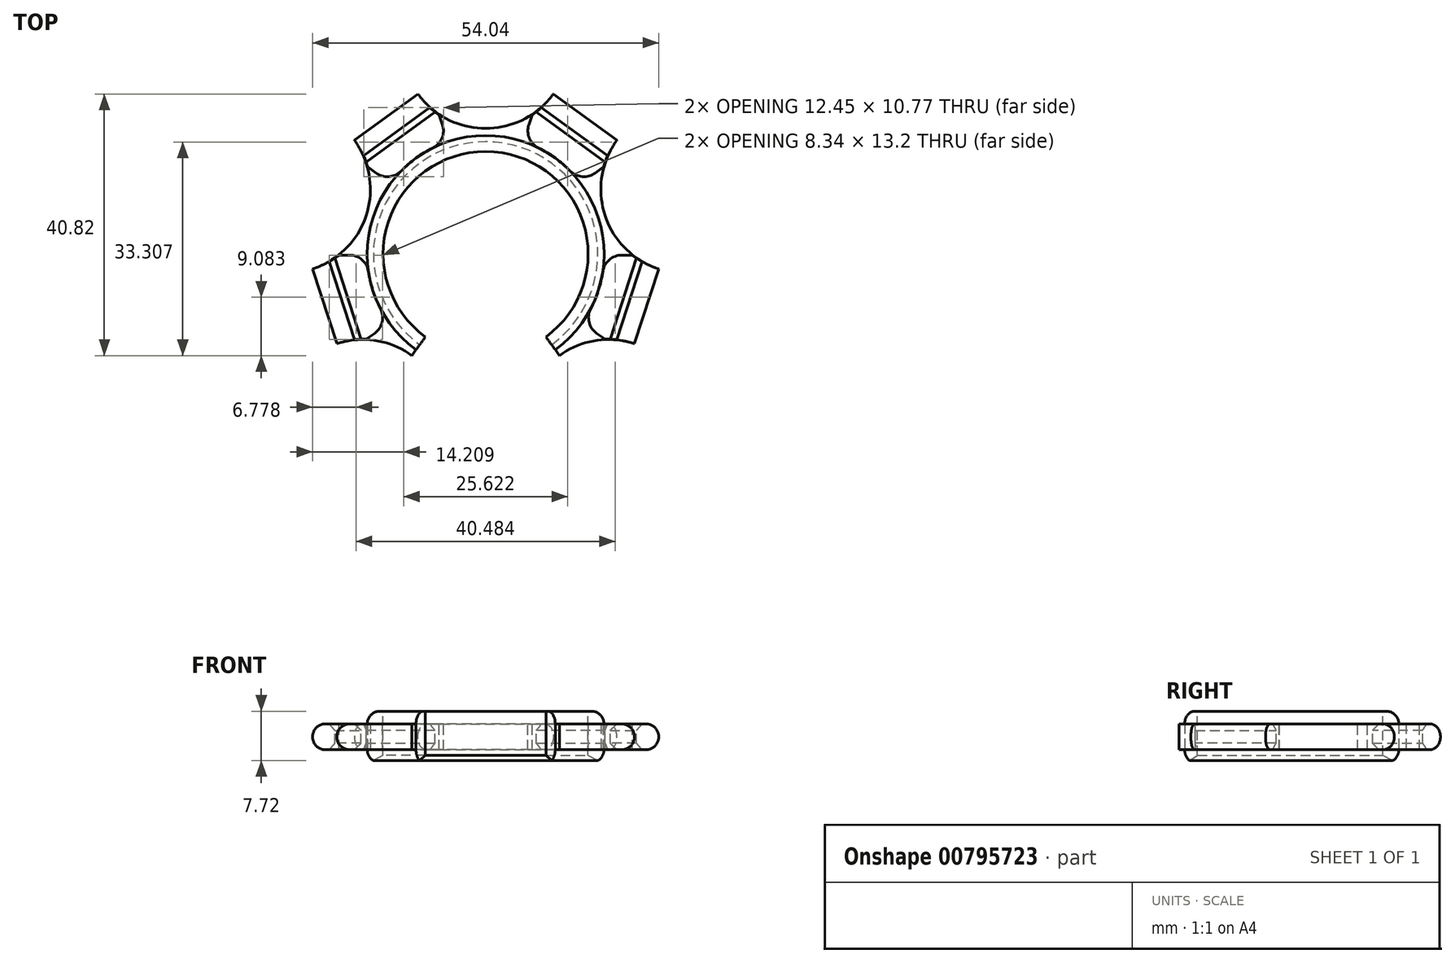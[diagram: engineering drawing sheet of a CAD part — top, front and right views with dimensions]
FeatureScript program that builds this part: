
annotation { "Feature Type Name" : "Feature", "Feature Type Description" : "" }
export const myFeature = defineFeature(function(context is Context, id is Id, definition is map)
    precondition{}
    {
        {
            var Q0;
            Q0=qCreatedBy(makeId("Top.planeOp"),FACE);
            var sketch = newSketch(context, id + "F0", { "sketchPlane" : qUnion([Q0])});
            skCircle(sketch, "E0.cCircle", {"center": v(0, 0) * mm, "radius": 52.24 * mm, "construction": true});
            skLineSegment(sketch, "E0.0", {"start": v(-37.95, 52.24) * mm, "end": v(37.95, 52.24) * mm});
            skLineSegment(sketch, "E0.1", {"start": v(37.95, 52.24) * mm, "end": v(61.41, -19.95) * mm});
            skLineSegment(sketch, "E0.2", {"start": v(61.41, -19.95) * mm, "end": v(0, -64.57) * mm});
            skLineSegment(sketch, "E0.3", {"start": v(0, -64.57) * mm, "end": v(-61.41, -19.95) * mm});
            skLineSegment(sketch, "E0.4", {"start": v(-61.41, -19.95) * mm, "end": v(-37.95, 52.24) * mm});
            skPoint(sketch, "E0.0.midPoint", {"position": v(0, 52.24) * mm});
            skLineSegment(sketch, "E1", {"start": v(0, 0) * mm, "end": v(-49.68, 16.14) * mm});
            skLineSegment(sketch, "E2", {"start": v(-49.68, 16.14) * mm, "end": v(0, 52.24) * mm});
            skLineSegment(sketch, "E3", {"start": v(0, 52.24) * mm, "end": v(0, 0) * mm});
            skLineSegment(sketch, "E4", {"start": v(0, 0) * mm, "end": v(49.68, 16.14) * mm});
            skLineSegment(sketch, "E5", {"start": v(49.68, 16.14) * mm, "end": v(0, 52.24) * mm});
            skLineSegment(sketch, "E6", {"start": v(49.68, 16.14) * mm, "end": v(30.7, -42.26) * mm});
            skLineSegment(sketch, "E7", {"start": v(30.7, -42.26) * mm, "end": v(0, 0) * mm});
            skLineSegment(sketch, "E8", {"start": v(0, 0) * mm, "end": v(-30.7, -42.26) * mm});
            skLineSegment(sketch, "E9", {"start": v(-30.7, -42.26) * mm, "end": v(-49.68, 16.14) * mm});
            skLineSegment(sketch, "E10", {"start": v(-30.7, -42.26) * mm, "end": v(30.7, -42.26) * mm});
            skLineSegment(sketch, "E11", {"start": v(0, 0) * mm, "end": v(61.41, -19.95) * mm});
            skLineSegment(sketch, "E12", {"start": v(0, 0) * mm, "end": v(37.95, 52.24) * mm});
            skLineSegment(sketch, "E13", {"start": v(0, 0) * mm, "end": v(-37.95, 52.24) * mm});
            skLineSegment(sketch, "E14", {"start": v(0, 0) * mm, "end": v(-61.41, -19.95) * mm});
            skLineSegment(sketch, "E15", {"start": v(0, -42.26) * mm, "end": v(0, -64.57) * mm});
            skLineSegment(sketch, "E16", {"start": v(0, 0) * mm, "end": v(-24.84, 8.07) * mm});
            skLineSegment(sketch, "E17", {"start": v(-24.84, 8.07) * mm, "end": v(-49.68, 16.14) * mm});
            skLineSegment(sketch, "E18", {"start": v(-37.26, 12.1) * mm, "end": v(-49.68, 16.14) * mm});
            skLineSegment(sketch, "E19", {"start": v(-37.26, 12.1) * mm, "end": v(-24.84, 8.07) * mm});
            skLineSegment(sketch, "E20", {"start": v(0, 0) * mm, "end": v(0, 26.12) * mm});
            skLineSegment(sketch, "E21", {"start": v(0, 26.12) * mm, "end": v(0, 52.24) * mm});
            skLineSegment(sketch, "E22", {"start": v(0, 39.18) * mm, "end": v(0, 52.24) * mm});
            skLineSegment(sketch, "E23", {"start": v(0, 39.18) * mm, "end": v(0, 26.12) * mm});
            skLineSegment(sketch, "E24", {"start": v(0, 0) * mm, "end": v(24.84, 8.07) * mm});
            skLineSegment(sketch, "E25", {"start": v(24.84, 8.07) * mm, "end": v(49.68, 16.14) * mm});
            skLineSegment(sketch, "E26", {"start": v(37.26, 12.1) * mm, "end": v(24.84, 8.07) * mm});
            skLineSegment(sketch, "E27", {"start": v(0, 0) * mm, "end": v(15.35, -21.13) * mm});
            skLineSegment(sketch, "E28", {"start": v(15.35, -21.13) * mm, "end": v(30.7, -42.26) * mm});
            skLineSegment(sketch, "E29", {"start": v(30.7, -42.26) * mm, "end": v(23.03, -31.7) * mm});
            skLineSegment(sketch, "E30", {"start": v(23.03, -31.7) * mm, "end": v(15.35, -21.13) * mm});
            skLineSegment(sketch, "E31", {"start": v(0, 0) * mm, "end": v(-15.35, -21.13) * mm});
            skLineSegment(sketch, "E32", {"start": v(-15.35, -21.13) * mm, "end": v(-30.7, -42.26) * mm});
            skLineSegment(sketch, "E33", {"start": v(-30.7, -42.26) * mm, "end": v(-23.03, -31.7) * mm});
            skLineSegment(sketch, "E34", {"start": v(-23.03, -31.7) * mm, "end": v(-15.35, -21.13) * mm});
            skLineSegment(sketch, "E35", {"start": v(-31.05, 10.09) * mm, "end": v(-43.47, 14.12) * mm});
            skLineSegment(sketch, "E36", {"start": v(0, 32.65) * mm, "end": v(0, 45.7) * mm});
            skLineSegment(sketch, "E37", {"start": v(37.26, 12.1) * mm, "end": v(49.68, 16.14) * mm});
            skLineSegment(sketch, "E38", {"start": v(31.05, 10.09) * mm, "end": v(43.47, 14.12) * mm});
            skLineSegment(sketch, "E39", {"start": v(30.7, -42.26) * mm, "end": v(26.87, -36.98) * mm});
            skLineSegment(sketch, "E40", {"start": v(-30.7, -42.26) * mm, "end": v(-26.87, -36.98) * mm});
            skCircle(sketch, "E41", {"center": v(-19.2, -26.41) * mm, "radius": 13.06 * mm});
            skCircle(sketch, "E42", {"center": v(-31.05, 10.09) * mm, "radius": 13.06 * mm});
            skCircle(sketch, "E43", {"center": v(0, 32.65) * mm, "radius": 13.06 * mm});
            skCircle(sketch, "E44", {"center": v(31.05, 10.09) * mm, "radius": 13.06 * mm});
            skCircle(sketch, "E45", {"center": v(19.2, -26.41) * mm, "radius": 13.06 * mm});
            skLineSegment(sketch, "E46", {"start": v(0, 0) * mm, "end": v(0, -42.26) * mm});
            skLineSegment(sketch, "E47", {"start": v(0, -42.26) * mm, "end": v(0, -21.13) * mm});
            skLineSegment(sketch, "E48", {"start": v(0, -21.13) * mm, "end": v(0, 0) * mm});
            skLineSegment(sketch, "E49", {"start": v(0, 0) * mm, "end": v(0, -10.57) * mm});
            skLineSegment(sketch, "E50", {"start": v(0, -10.57) * mm, "end": v(0, -21.13) * mm});
            skLineSegment(sketch, "E51", {"start": v(0, -15.85) * mm, "end": v(0, -21.13) * mm});
            skLineSegment(sketch, "E52", {"start": v(0, -15.85) * mm, "end": v(0, -18.49) * mm});
            skLineSegment(sketch, "E53", {"start": v(0, -18.49) * mm, "end": v(0, 0) * mm});
            skCircle(sketch, "E54", {"center": v(0, 0) * mm, "radius": 18.49 * mm});
            skLineSegment(sketch, "E55", {"start": v(-19.2, -26.41) * mm, "end": v(-31.05, 10.09) * mm});
            skLineSegment(sketch, "E56", {"start": v(-31.05, 10.09) * mm, "end": v(0, 32.65) * mm});
            skLineSegment(sketch, "E57", {"start": v(0, 32.65) * mm, "end": v(31.05, 10.09) * mm});
            skLineSegment(sketch, "E58", {"start": v(31.05, 10.09) * mm, "end": v(19.2, -26.41) * mm});
            skLineSegment(sketch, "E59", {"start": v(19.2, -26.41) * mm, "end": v(-19.2, -26.41) * mm});
            skSolve(sketch);
        }
        {
            var Q0;
            {var subQ0=sQuery(id+"F0.wireOp",EDGE,"E19");Q0=makeQuery(id+"F0.imprint","IMPRINT",FACE,{"disambiguationData":[TD([[makeQuery(id+"F0.imprint","IMPRINT",EDGE,{"derivedFrom":subQ0}),-1.0]])]});}
            var Q1;
            {var subQ0=sQuery(id+"F0.wireOp",EDGE,"E19");Q1=makeQuery(id+"F0.imprint","IMPRINT",FACE,{"disambiguationData":[TD([[makeQuery(id+"F0.imprint","IMPRINT",EDGE,{"derivedFrom":subQ0}),1.0]])]});}
            var Q2;
            {var subQ0=sQuery(id+"F0.wireOp",EDGE,"E35");Q2=makeQuery(id+"F0.imprint","IMPRINT",FACE,{"disambiguationData":[TD([[makeQuery(id+"F0.imprint","IMPRINT",EDGE,{"derivedFrom":subQ0}),-1.0]])]});}
            var Q3;
            {var subQ0=sQuery(id+"F0.wireOp",EDGE,"E35");Q3=makeQuery(id+"F0.imprint","IMPRINT",FACE,{"disambiguationData":[TD([[makeQuery(id+"F0.imprint","IMPRINT",EDGE,{"derivedFrom":subQ0}),1.0]])]});}
            var Q4;
            {var subQ0=sQuery(id+"F0.wireOp",EDGE,"E36");Q4=makeQuery(id+"F0.imprint","IMPRINT",FACE,{"disambiguationData":[TD([[makeQuery(id+"F0.imprint","IMPRINT",EDGE,{"derivedFrom":subQ0}),1.0]])]});}
            var Q5;
            {var subQ0=sQuery(id+"F0.wireOp",EDGE,"E36");Q5=makeQuery(id+"F0.imprint","IMPRINT",FACE,{"disambiguationData":[TD([[makeQuery(id+"F0.imprint","IMPRINT",EDGE,{"derivedFrom":subQ0}),-1.0]])]});}
            var Q6;
            {var subQ0=sQuery(id+"F0.wireOp",EDGE,"E23");Q6=makeQuery(id+"F0.imprint","IMPRINT",FACE,{"disambiguationData":[TD([[makeQuery(id+"F0.imprint","IMPRINT",EDGE,{"derivedFrom":subQ0}),1.0]])]});}
            var Q7;
            {var subQ0=sQuery(id+"F0.wireOp",EDGE,"E23");Q7=makeQuery(id+"F0.imprint","IMPRINT",FACE,{"disambiguationData":[TD([[makeQuery(id+"F0.imprint","IMPRINT",EDGE,{"derivedFrom":subQ0}),-1.0]])]});}
            var Q8;
            {var subQ0=sQuery(id+"F0.wireOp",EDGE,"E26");Q8=makeQuery(id+"F0.imprint","IMPRINT",FACE,{"disambiguationData":[TD([[makeQuery(id+"F0.imprint","IMPRINT",EDGE,{"derivedFrom":subQ0}),-1.0]])]});}
            var Q9;
            {var subQ0=sQuery(id+"F0.wireOp",EDGE,"E38");Q9=makeQuery(id+"F0.imprint","IMPRINT",FACE,{"disambiguationData":[TD([[makeQuery(id+"F0.imprint","IMPRINT",EDGE,{"derivedFrom":subQ0}),1.0]])]});}
            var Q10;
            {var subQ0=sQuery(id+"F0.wireOp",EDGE,"E38");Q10=makeQuery(id+"F0.imprint","IMPRINT",FACE,{"disambiguationData":[TD([[makeQuery(id+"F0.imprint","IMPRINT",EDGE,{"derivedFrom":subQ0}),-1.0]])]});}
            var Q11;
            {var subQ0=sQuery(id+"F0.wireOp",EDGE,"E26");Q11=makeQuery(id+"F0.imprint","IMPRINT",FACE,{"disambiguationData":[TD([[makeQuery(id+"F0.imprint","IMPRINT",EDGE,{"derivedFrom":subQ0}),1.0]])]});}
            var Q12;
            {var subQ0=sQuery(id+"F0.wireOp",EDGE,"E30");var subQ1=sQuery(id+"F0.wireOp",EDGE,"E27");var subQ2=makeQuery(id+"F0.imprint","INTERSECT",VERTEX,{"derivedFrom":[subQ1,subQ0]});Q12=makeQuery(id+"F0.imprint","IMPRINT",FACE,{"disambiguationData":[TD([[makeQuery(id+"F0.imprint","IMPRINT",EDGE,{"disambiguationData":[TD([[subQ2,1.0]])],"derivedFrom":subQ1}),1.0]])]});}
            var Q13;
            {var subQ0=sQuery(id+"F0.wireOp",EDGE,"E30");var subQ1=sQuery(id+"F0.wireOp",EDGE,"E27");var subQ2=makeQuery(id+"F0.imprint","INTERSECT",VERTEX,{"derivedFrom":[subQ1,subQ0]});Q13=makeQuery(id+"F0.imprint","IMPRINT",FACE,{"disambiguationData":[TD([[makeQuery(id+"F0.imprint","IMPRINT",EDGE,{"disambiguationData":[TD([[subQ2,1.0]])],"derivedFrom":subQ1}),-1.0]])]});}
            var Q14;
            {var subQ0=sQuery(id+"F0.wireOp",EDGE,"E29");Q14=makeQuery(id+"F0.imprint","IMPRINT",FACE,{"disambiguationData":[TD([[makeQuery(id+"F0.imprint","IMPRINT",EDGE,{"derivedFrom":subQ0}),1.0]])]});}
            var Q15;
            {var subQ0=sQuery(id+"F0.wireOp",EDGE,"E29");Q15=makeQuery(id+"F0.imprint","IMPRINT",FACE,{"disambiguationData":[TD([[makeQuery(id+"F0.imprint","IMPRINT",EDGE,{"derivedFrom":subQ0}),-1.0]])]});}
            var Q16;
            {var subQ0=sQuery(id+"F0.wireOp",EDGE,"E33");Q16=makeQuery(id+"F0.imprint","IMPRINT",FACE,{"disambiguationData":[TD([[makeQuery(id+"F0.imprint","IMPRINT",EDGE,{"derivedFrom":subQ0}),-1.0]])]});}
            var Q17;
            {var subQ0=sQuery(id+"F0.wireOp",EDGE,"E34");var subQ1=sQuery(id+"F0.wireOp",EDGE,"E31");var subQ2=makeQuery(id+"F0.imprint","INTERSECT",VERTEX,{"derivedFrom":[subQ1,subQ0]});Q17=makeQuery(id+"F0.imprint","IMPRINT",FACE,{"disambiguationData":[TD([[makeQuery(id+"F0.imprint","IMPRINT",EDGE,{"disambiguationData":[TD([[subQ2,1.0]])],"derivedFrom":subQ1}),1.0]])]});}
            var Q18;
            {var subQ0=sQuery(id+"F0.wireOp",EDGE,"E34");var subQ1=sQuery(id+"F0.wireOp",EDGE,"E31");var subQ2=makeQuery(id+"F0.imprint","INTERSECT",VERTEX,{"derivedFrom":[subQ1,subQ0]});Q18=makeQuery(id+"F0.imprint","IMPRINT",FACE,{"disambiguationData":[TD([[makeQuery(id+"F0.imprint","IMPRINT",EDGE,{"disambiguationData":[TD([[subQ2,1.0]])],"derivedFrom":subQ1}),-1.0]])]});}
            var Q19;
            {var subQ0=sQuery(id+"F0.wireOp",EDGE,"E33");Q19=makeQuery(id+"F0.imprint","IMPRINT",FACE,{"disambiguationData":[TD([[makeQuery(id+"F0.imprint","IMPRINT",EDGE,{"derivedFrom":subQ0}),1.0]])]});}
            var Q20;
            {var subQ0=sQuery(id+"F0.wireOp",EDGE,"E53");var subQ6=makeQuery(id+"F0.imprint","IMPRINT",VERTEX,{"derivedFrom":subQ0});Q20=makeQuery(id+"F0.imprint","IMPRINT",FACE,{"disambiguationData":[TD([[makeQuery(id+"F0.imprint","IMPRINT",EDGE,{"disambiguationData":[TD([[subQ6,1.0]])],"derivedFrom":subQ0}),1.0]])]});}
            var Q21;
            {var subQ1=sQuery(id+"F0.wireOp",EDGE,"E11");var subQ3=sQuery(id+"F0.wireOp",EDGE,"E54");var subQ4=makeQuery(id+"F0.imprint","INTERSECT",VERTEX,{"derivedFrom":[subQ1,subQ3]});Q21=makeQuery(id+"F0.imprint","IMPRINT",FACE,{"disambiguationData":[TD([[makeQuery(id+"F0.imprint","IMPRINT",EDGE,{"disambiguationData":[TD([[subQ4,1.0]])],"derivedFrom":subQ3}),1.0]])]});}
            var Q22;
            {var subQ1=sQuery(id+"F0.wireOp",EDGE,"E12");var subQ3=sQuery(id+"F0.wireOp",EDGE,"E54");var subQ4=makeQuery(id+"F0.imprint","INTERSECT",VERTEX,{"derivedFrom":[subQ1,subQ3]});Q22=makeQuery(id+"F0.imprint","IMPRINT",FACE,{"disambiguationData":[TD([[makeQuery(id+"F0.imprint","IMPRINT",EDGE,{"disambiguationData":[TD([[subQ4,1.0]])],"derivedFrom":subQ3}),1.0]])]});}
            var Q23;
            {var subQ1=sQuery(id+"F0.wireOp",EDGE,"E13");var subQ3=sQuery(id+"F0.wireOp",EDGE,"E54");var subQ4=makeQuery(id+"F0.imprint","INTERSECT",VERTEX,{"derivedFrom":[subQ1,subQ3]});Q23=makeQuery(id+"F0.imprint","IMPRINT",FACE,{"disambiguationData":[TD([[makeQuery(id+"F0.imprint","IMPRINT",EDGE,{"disambiguationData":[TD([[subQ4,1.0]])],"derivedFrom":subQ3}),1.0]])]});}
            var Q24;
            {var subQ1=sQuery(id+"F0.wireOp",EDGE,"E14");var subQ3=sQuery(id+"F0.wireOp",EDGE,"E54");var subQ4=makeQuery(id+"F0.imprint","INTERSECT",VERTEX,{"derivedFrom":[subQ1,subQ3]});Q24=makeQuery(id+"F0.imprint","IMPRINT",FACE,{"disambiguationData":[TD([[makeQuery(id+"F0.imprint","IMPRINT",EDGE,{"disambiguationData":[TD([[subQ4,1.0]])],"derivedFrom":subQ3}),1.0]])]});}
            var Q25;
            {var subQ1=sQuery(id+"F0.wireOp",EDGE,"E11");var subQ3=sQuery(id+"F0.wireOp",EDGE,"E54");var subQ4=makeQuery(id+"F0.imprint","INTERSECT",VERTEX,{"derivedFrom":[subQ1,subQ3]});Q25=makeQuery(id+"F0.imprint","IMPRINT",FACE,{"disambiguationData":[TD([[makeQuery(id+"F0.imprint","IMPRINT",EDGE,{"disambiguationData":[TD([[subQ4,-1.0]])],"derivedFrom":subQ3}),1.0]])]});}
            var Q26;
            {var subQ1=sQuery(id+"F0.wireOp",EDGE,"E12");var subQ3=sQuery(id+"F0.wireOp",EDGE,"E54");var subQ4=makeQuery(id+"F0.imprint","INTERSECT",VERTEX,{"derivedFrom":[subQ1,subQ3]});Q26=makeQuery(id+"F0.imprint","IMPRINT",FACE,{"disambiguationData":[TD([[makeQuery(id+"F0.imprint","IMPRINT",EDGE,{"disambiguationData":[TD([[subQ4,-1.0]])],"derivedFrom":subQ3}),1.0]])]});}
            var Q27;
            {var subQ1=sQuery(id+"F0.wireOp",EDGE,"E13");var subQ3=sQuery(id+"F0.wireOp",EDGE,"E54");var subQ4=makeQuery(id+"F0.imprint","INTERSECT",VERTEX,{"derivedFrom":[subQ1,subQ3]});Q27=makeQuery(id+"F0.imprint","IMPRINT",FACE,{"disambiguationData":[TD([[makeQuery(id+"F0.imprint","IMPRINT",EDGE,{"disambiguationData":[TD([[subQ4,-1.0]])],"derivedFrom":subQ3}),1.0]])]});}
            var Q28;
            {var subQ1=sQuery(id+"F0.wireOp",EDGE,"E14");var subQ3=sQuery(id+"F0.wireOp",EDGE,"E54");var subQ4=makeQuery(id+"F0.imprint","INTERSECT",VERTEX,{"derivedFrom":[subQ1,subQ3]});Q28=makeQuery(id+"F0.imprint","IMPRINT",FACE,{"disambiguationData":[TD([[makeQuery(id+"F0.imprint","IMPRINT",EDGE,{"disambiguationData":[TD([[subQ4,-1.0]])],"derivedFrom":subQ3}),1.0]])]});}
            var Q29;
            {var subQ0=sQuery(id+"F0.wireOp",EDGE,"E53");var subQ6=makeQuery(id+"F0.imprint","IMPRINT",VERTEX,{"derivedFrom":subQ0});Q29=makeQuery(id+"F0.imprint","IMPRINT",FACE,{"disambiguationData":[TD([[makeQuery(id+"F0.imprint","IMPRINT",EDGE,{"disambiguationData":[TD([[subQ6,1.0]])],"derivedFrom":subQ0}),-1.0]])]});}
            extrude(context, id + "F1", {"entities" : qUnion([Q0, Q1, Q2, Q3, Q4, Q5, Q6, Q7, Q8, Q9, Q10, Q11, Q12, Q13, Q14, Q15, Q16, Q17, Q18, Q19, Q20, Q21, Q22, Q23, Q24, Q25, Q26, Q27, Q28, Q29]), "depth" : 4 * mm, "offsetDistance" : 25 * mm, "hasSecondDirection" : true, "secondDirectionOppositeDirection" : true, "secondDirectionDepth" : 4 * mm});
        }
        {
            var Q0;
            {var subQ0=sQuery(id+"F0.wireOp",EDGE,"E54");var subQ1=sQuery(id+"F0.wireOp",EDGE,"E13");var subQ2=makeQuery(id+"F0.imprint","INTERSECT",VERTEX,{"derivedFrom":[subQ1,subQ0]});Q0=makeQuery(id+"F0.imprint","IMPRINT",FACE,{"disambiguationData":[TD([[makeQuery(id+"F0.imprint","IMPRINT",EDGE,{"disambiguationData":[TD([[subQ2,-1.0]])],"derivedFrom":subQ1}),1.0]])]});}
            var Q1;
            {var subQ0=sQuery(id+"F0.wireOp",EDGE,"E54");var subQ1=sQuery(id+"F0.wireOp",EDGE,"E13");var subQ2=makeQuery(id+"F0.imprint","INTERSECT",VERTEX,{"derivedFrom":[subQ1,subQ0]});Q1=makeQuery(id+"F0.imprint","IMPRINT",FACE,{"disambiguationData":[TD([[makeQuery(id+"F0.imprint","IMPRINT",EDGE,{"disambiguationData":[TD([[subQ2,-1.0]])],"derivedFrom":subQ1}),-1.0]])]});}
            var Q2;
            {var subQ5=sQuery(id+"F0.wireOp",EDGE,"E54");var subQ7=sQuery(id+"F0.wireOp",EDGE,"E12");var subQ8=makeQuery(id+"F0.imprint","INTERSECT",VERTEX,{"derivedFrom":[subQ7,subQ5]});Q2=makeQuery(id+"F0.imprint","IMPRINT",FACE,{"disambiguationData":[TD([[makeQuery(id+"F0.imprint","IMPRINT",EDGE,{"disambiguationData":[TD([[subQ8,-1.0]])],"derivedFrom":subQ7}),1.0]])]});}
            var Q3;
            {var subQ0=sQuery(id+"F0.wireOp",EDGE,"E54");var subQ1=sQuery(id+"F0.wireOp",EDGE,"E12");var subQ2=makeQuery(id+"F0.imprint","INTERSECT",VERTEX,{"derivedFrom":[subQ1,subQ0]});Q3=makeQuery(id+"F0.imprint","IMPRINT",FACE,{"disambiguationData":[TD([[makeQuery(id+"F0.imprint","IMPRINT",EDGE,{"disambiguationData":[TD([[subQ2,-1.0]])],"derivedFrom":subQ1}),-1.0]])]});}
            var Q4;
            {var subQ0=sQuery(id+"F0.wireOp",EDGE,"E54");var subQ1=sQuery(id+"F0.wireOp",EDGE,"E11");var subQ2=makeQuery(id+"F0.imprint","INTERSECT",VERTEX,{"derivedFrom":[subQ1,subQ0]});Q4=makeQuery(id+"F0.imprint","IMPRINT",FACE,{"disambiguationData":[TD([[makeQuery(id+"F0.imprint","IMPRINT",EDGE,{"disambiguationData":[TD([[subQ2,-1.0]])],"derivedFrom":subQ1}),1.0]])]});}
            var Q5;
            {var subQ5=sQuery(id+"F0.wireOp",EDGE,"E54");var subQ7=sQuery(id+"F0.wireOp",EDGE,"E11");var subQ9=makeQuery(id+"F0.imprint","INTERSECT",VERTEX,{"derivedFrom":[subQ7,subQ5]});Q5=makeQuery(id+"F0.imprint","IMPRINT",FACE,{"disambiguationData":[TD([[makeQuery(id+"F0.imprint","IMPRINT",EDGE,{"disambiguationData":[TD([[subQ9,-1.0]])],"derivedFrom":subQ7}),-1.0]])]});}
            var Q6;
            {var subQ0=sQuery(id+"F0.wireOp",EDGE,"E51");Q6=makeQuery(id+"F0.imprint","IMPRINT",FACE,{"disambiguationData":[TD([[makeQuery(id+"F0.imprint","IMPRINT",EDGE,{"derivedFrom":subQ0}),1.0]])]});}
            var Q7;
            {var subQ0=sQuery(id+"F0.wireOp",EDGE,"E51");Q7=makeQuery(id+"F0.imprint","IMPRINT",FACE,{"disambiguationData":[TD([[makeQuery(id+"F0.imprint","IMPRINT",EDGE,{"derivedFrom":subQ0}),-1.0]])]});}
            var Q8;
            {var subQ0=sQuery(id+"F0.wireOp",EDGE,"E54");var subQ1=sQuery(id+"F0.wireOp",EDGE,"E14");var subQ2=makeQuery(id+"F0.imprint","INTERSECT",VERTEX,{"derivedFrom":[subQ1,subQ0]});Q8=makeQuery(id+"F0.imprint","IMPRINT",FACE,{"disambiguationData":[TD([[makeQuery(id+"F0.imprint","IMPRINT",EDGE,{"disambiguationData":[TD([[subQ2,-1.0]])],"derivedFrom":subQ1}),1.0]])]});}
            var Q9;
            {var subQ5=sQuery(id+"F0.wireOp",EDGE,"E54");var subQ6=sQuery(id+"F0.wireOp",EDGE,"E14");var subQ7=makeQuery(id+"F0.imprint","INTERSECT",VERTEX,{"derivedFrom":[subQ6,subQ5]});Q9=makeQuery(id+"F0.imprint","IMPRINT",FACE,{"disambiguationData":[TD([[makeQuery(id+"F0.imprint","IMPRINT",EDGE,{"disambiguationData":[TD([[subQ7,-1.0]])],"derivedFrom":subQ6}),-1.0]])]});}
            extrude(context, id + "F2", {"entities" : qUnion([Q0, Q1, Q2, Q3, Q4, Q5, Q6, Q7, Q8, Q9]), "depth" : 2 * mm, "offsetDistance" : 25 * mm, "hasSecondDirection" : true, "secondDirectionOppositeDirection" : true, "secondDirectionDepth" : 2 * mm});
        }
        {
            var Q0;
            Q0=qCreatedBy(makeId("Top.planeOp"),FACE);
            cPlane(context, id + "F3", {"entities" : qUnion([Q0]), "cplaneType" : CPlaneType.OFFSET, "offset" : 4 * mm, "width" : 150 * mm, "height" : 150 * mm});
        }
        {
            var Q0;
            Q0=qCreatedBy(id+"F3.planeOp",FACE);
            var sketch = newSketch(context, id + "F4", { "sketchPlane" : qUnion([Q0])});
            skCircle(sketch, "E60.cCircle", {"center": v(0, 0) * mm, "radius": 32.5 * mm, "construction": true});
            skLineSegment(sketch, "E60.0", {"start": v(0, 32.5) * mm, "end": v(30.9, 10.04) * mm});
            skLineSegment(sketch, "E60.1", {"start": v(30.9, 10.04) * mm, "end": v(19.1, -26.3) * mm});
            skLineSegment(sketch, "E60.2", {"start": v(19.1, -26.3) * mm, "end": v(-19.1, -26.3) * mm});
            skLineSegment(sketch, "E60.3", {"start": v(-19.1, -26.3) * mm, "end": v(-30.9, 10.04) * mm});
            skLineSegment(sketch, "E60.4", {"start": v(-30.9, 10.04) * mm, "end": v(0, 32.5) * mm});
            skLineSegment(sketch, "E61", {"start": v(0, 32.5) * mm, "end": v(0, 0) * mm});
            skLineSegment(sketch, "E62", {"start": v(0, 0) * mm, "end": v(-30.9, 10.04) * mm});
            skLineSegment(sketch, "E63", {"start": v(0, 0) * mm, "end": v(-19.1, -26.3) * mm});
            skLineSegment(sketch, "E64", {"start": v(19.1, -26.3) * mm, "end": v(0, 0) * mm});
            skLineSegment(sketch, "E65", {"start": v(30.9, 10.04) * mm, "end": v(0, 0) * mm});
            skCircle(sketch, "E66", {"center": v(0, 0) * mm, "radius": 18.5 * mm});
            skCircle(sketch, "E67", {"center": v(0, 0) * mm, "radius": 16 * mm});
            skCircle(sketch, "E68.cCircle", {"center": v(-30.9, 10.04) * mm, "radius": 10.5 * mm, "construction": true});
            skLineSegment(sketch, "E68.0", {"start": v(-20.92, 6.8) * mm, "end": v(-28.73, -0.23) * mm});
            skLineSegment(sketch, "E68.1", {"start": v(-28.73, -0.23) * mm, "end": v(-38.71, 3.02) * mm});
            skLineSegment(sketch, "E68.2", {"start": v(-38.71, 3.02) * mm, "end": v(-40.9, 13.29) * mm});
            skLineSegment(sketch, "E68.3", {"start": v(-40.9, 13.29) * mm, "end": v(-33.1, 20.31) * mm});
            skLineSegment(sketch, "E68.4", {"start": v(-33.1, 20.31) * mm, "end": v(-23.1, 17.07) * mm});
            skLineSegment(sketch, "E68.5", {"start": v(-23.1, 17.07) * mm, "end": v(-20.92, 6.8) * mm});
            skCircle(sketch, "E69.cCircle", {"center": v(0, 32.5) * mm, "radius": 10.5 * mm, "construction": true});
            skLineSegment(sketch, "E69.0", {"start": v(0, 22) * mm, "end": v(-9.1, 27.25) * mm});
            skLineSegment(sketch, "E69.1", {"start": v(-9.1, 27.25) * mm, "end": v(-9.1, 37.75) * mm});
            skLineSegment(sketch, "E69.2", {"start": v(-9.1, 37.75) * mm, "end": v(0, 43) * mm});
            skLineSegment(sketch, "E69.3", {"start": v(0, 43) * mm, "end": v(9.1, 37.75) * mm});
            skLineSegment(sketch, "E69.4", {"start": v(9.1, 37.75) * mm, "end": v(9.1, 27.25) * mm});
            skLineSegment(sketch, "E69.5", {"start": v(9.1, 27.25) * mm, "end": v(0, 22) * mm});
            skCircle(sketch, "E70.cCircle", {"center": v(30.9, 10.04) * mm, "radius": 10.5 * mm, "construction": true});
            skLineSegment(sketch, "E70.0", {"start": v(20.92, 6.8) * mm, "end": v(23.1, 17.07) * mm});
            skLineSegment(sketch, "E70.1", {"start": v(23.1, 17.07) * mm, "end": v(33.1, 20.31) * mm});
            skLineSegment(sketch, "E70.2", {"start": v(33.1, 20.31) * mm, "end": v(40.9, 13.29) * mm});
            skLineSegment(sketch, "E70.3", {"start": v(40.9, 13.29) * mm, "end": v(38.71, 3.02) * mm});
            skLineSegment(sketch, "E70.4", {"start": v(38.71, 3.02) * mm, "end": v(28.73, -0.23) * mm});
            skLineSegment(sketch, "E70.5", {"start": v(28.73, -0.23) * mm, "end": v(20.92, 6.8) * mm});
            skCircle(sketch, "E71.cCircle", {"center": v(19.1, -26.3) * mm, "radius": 10.5 * mm, "construction": true});
            skLineSegment(sketch, "E71.0", {"start": v(12.93, -17.8) * mm, "end": v(23.37, -16.7) * mm});
            skLineSegment(sketch, "E71.1", {"start": v(23.37, -16.7) * mm, "end": v(29.55, -25.2) * mm});
            skLineSegment(sketch, "E71.2", {"start": v(29.55, -25.2) * mm, "end": v(25.27, -34.79) * mm});
            skLineSegment(sketch, "E71.3", {"start": v(25.27, -34.79) * mm, "end": v(14.83, -35.89) * mm});
            skLineSegment(sketch, "E71.4", {"start": v(14.83, -35.89) * mm, "end": v(8.66, -27.4) * mm});
            skLineSegment(sketch, "E71.5", {"start": v(8.66, -27.4) * mm, "end": v(12.93, -17.8) * mm});
            skCircle(sketch, "E72.cCircle", {"center": v(-19.1, -26.3) * mm, "radius": 10.5 * mm, "construction": true});
            skLineSegment(sketch, "E72.0", {"start": v(-12.93, -17.8) * mm, "end": v(-8.66, -27.4) * mm});
            skLineSegment(sketch, "E72.1", {"start": v(-8.66, -27.4) * mm, "end": v(-14.83, -35.89) * mm});
            skLineSegment(sketch, "E72.2", {"start": v(-14.83, -35.89) * mm, "end": v(-25.27, -34.79) * mm});
            skLineSegment(sketch, "E72.3", {"start": v(-25.27, -34.79) * mm, "end": v(-29.55, -25.2) * mm});
            skLineSegment(sketch, "E72.4", {"start": v(-29.55, -25.2) * mm, "end": v(-23.37, -16.7) * mm});
            skLineSegment(sketch, "E72.5", {"start": v(-23.37, -16.7) * mm, "end": v(-12.93, -17.8) * mm});
            skLineSegment(sketch, "E73", {"start": v(23.1, 17.07) * mm, "end": v(0, 0) * mm});
            skLineSegment(sketch, "E74", {"start": v(0, 0) * mm, "end": v(28.73, -0.23) * mm});
            skLineSegment(sketch, "E75", {"start": v(23.37, -16.7) * mm, "end": v(0, 0) * mm});
            skLineSegment(sketch, "E76", {"start": v(0, 0) * mm, "end": v(8.66, -27.4) * mm});
            skLineSegment(sketch, "E77", {"start": v(-8.66, -27.4) * mm, "end": v(0, 0) * mm});
            skLineSegment(sketch, "E78", {"start": v(-23.37, -16.7) * mm, "end": v(0, 0) * mm});
            skLineSegment(sketch, "E79", {"start": v(0, 0) * mm, "end": v(-28.73, -0.23) * mm});
            skLineSegment(sketch, "E80", {"start": v(-23.1, 17.07) * mm, "end": v(0, 0) * mm});
            skLineSegment(sketch, "E81", {"start": v(0, 0) * mm, "end": v(-9.1, 27.25) * mm});
            skLineSegment(sketch, "E82", {"start": v(0, 0) * mm, "end": v(9.1, 27.25) * mm});
            skLineSegment(sketch, "E83", {"start": v(4.55, 24.62) * mm, "end": v(22.01, 11.93) * mm});
            skLineSegment(sketch, "E84", {"start": v(22.01, 11.93) * mm, "end": v(24.82, 3.29) * mm});
            skLineSegment(sketch, "E85", {"start": v(24.82, 3.29) * mm, "end": v(18.15, -17.25) * mm});
            skLineSegment(sketch, "E86", {"start": v(18.15, -17.25) * mm, "end": v(10.8, -22.6) * mm});
            skLineSegment(sketch, "E87", {"start": v(10.8, -22.6) * mm, "end": v(-10.8, -22.6) * mm});
            skLineSegment(sketch, "E88", {"start": v(-10.8, -22.6) * mm, "end": v(-18.15, -17.25) * mm});
            skLineSegment(sketch, "E89", {"start": v(-18.15, -17.25) * mm, "end": v(-24.82, 3.29) * mm});
            skLineSegment(sketch, "E90", {"start": v(-24.82, 3.29) * mm, "end": v(-22.01, 11.93) * mm});
            skLineSegment(sketch, "E91", {"start": v(-22.01, 11.93) * mm, "end": v(-4.55, 24.62) * mm});
            skLineSegment(sketch, "E92", {"start": v(-4.55, 24.62) * mm, "end": v(4.55, 24.62) * mm});
            skCircle(sketch, "E93", {"center": v(-30.9, 10.04) * mm, "radius": 13 * mm});
            skCircle(sketch, "E94", {"center": v(0, 32.5) * mm, "radius": 13 * mm});
            skCircle(sketch, "E95", {"center": v(30.9, 10.04) * mm, "radius": 13 * mm});
            skCircle(sketch, "E96", {"center": v(19.1, -26.3) * mm, "radius": 13 * mm});
            skCircle(sketch, "E97", {"center": v(-19.1, -26.3) * mm, "radius": 13 * mm});
            skSolve(sketch);
        }
        {
            var Q0;
            {var subQ0=sQuery(id+"F4.wireOp",EDGE,"E68.1");Q0=makeQuery(id+"F4.imprint","IMPRINT",FACE,{"disambiguationData":[TD([[makeQuery(id+"F4.imprint","IMPRINT",EDGE,{"derivedFrom":subQ0}),-1.0]])]});}
            var Q1;
            {var subQ1=sQuery(id+"F4.wireOp",EDGE,"E60.4");var subQ3=sQuery(id+"F4.wireOp",EDGE,"E68.5");var subQ4=makeQuery(id+"F4.imprint","INTERSECT",VERTEX,{"derivedFrom":[subQ1,subQ3]});Q1=makeQuery(id+"F4.imprint","IMPRINT",FACE,{"disambiguationData":[TD([[makeQuery(id+"F4.imprint","IMPRINT",EDGE,{"disambiguationData":[TD([[subQ4,1.0]])],"derivedFrom":subQ1}),-1.0]])]});}
            var Q2;
            {var subQ1=sQuery(id+"F4.wireOp",EDGE,"E60.3");var subQ3=sQuery(id+"F4.wireOp",EDGE,"E68.0");var subQ4=makeQuery(id+"F4.imprint","INTERSECT",VERTEX,{"derivedFrom":[subQ1,subQ3]});Q2=makeQuery(id+"F4.imprint","IMPRINT",FACE,{"disambiguationData":[TD([[makeQuery(id+"F4.imprint","IMPRINT",EDGE,{"disambiguationData":[TD([[subQ4,-1.0]])],"derivedFrom":subQ1}),-1.0]])]});}
            var Q3;
            {var subQ1=sQuery(id+"F4.wireOp",EDGE,"E62");var subQ3=sQuery(id+"F4.wireOp",EDGE,"E90");var subQ4=makeQuery(id+"F4.imprint","INTERSECT",VERTEX,{"derivedFrom":[subQ1,subQ3]});Q3=makeQuery(id+"F4.imprint","IMPRINT",FACE,{"disambiguationData":[TD([[makeQuery(id+"F4.imprint","IMPRINT",EDGE,{"disambiguationData":[TD([[subQ4,1.0]])],"derivedFrom":subQ1}),1.0]])]});}
            var Q4;
            {var subQ1=sQuery(id+"F4.wireOp",EDGE,"E62");var subQ3=sQuery(id+"F4.wireOp",EDGE,"E90");var subQ4=makeQuery(id+"F4.imprint","INTERSECT",VERTEX,{"derivedFrom":[subQ1,subQ3]});Q4=makeQuery(id+"F4.imprint","IMPRINT",FACE,{"disambiguationData":[TD([[makeQuery(id+"F4.imprint","IMPRINT",EDGE,{"disambiguationData":[TD([[subQ4,1.0]])],"derivedFrom":subQ1}),-1.0]])]});}
            var Q5;
            {var subQ1=sQuery(id+"F4.wireOp",EDGE,"E62");var subQ3=sQuery(id+"F4.wireOp",EDGE,"E67");var subQ4=makeQuery(id+"F4.imprint","INTERSECT",VERTEX,{"derivedFrom":[subQ1,subQ3]});Q5=makeQuery(id+"F4.imprint","IMPRINT",FACE,{"disambiguationData":[TD([[makeQuery(id+"F4.imprint","IMPRINT",EDGE,{"disambiguationData":[TD([[subQ4,-1.0]])],"derivedFrom":subQ3}),1.0]])]});}
            var Q6;
            {var subQ1=sQuery(id+"F4.wireOp",EDGE,"E62");var subQ3=sQuery(id+"F4.wireOp",EDGE,"E67");var subQ4=makeQuery(id+"F4.imprint","INTERSECT",VERTEX,{"derivedFrom":[subQ1,subQ3]});Q6=makeQuery(id+"F4.imprint","IMPRINT",FACE,{"disambiguationData":[TD([[makeQuery(id+"F4.imprint","IMPRINT",EDGE,{"disambiguationData":[TD([[subQ4,1.0]])],"derivedFrom":subQ3}),1.0]])]});}
            var Q7;
            {var subQ0=sQuery(id+"F4.wireOp",EDGE,"E81");var subQ1=sQuery(id+"F4.wireOp",EDGE,"E67");var subQ2=makeQuery(id+"F4.imprint","INTERSECT",VERTEX,{"derivedFrom":[subQ1,subQ0]});Q7=makeQuery(id+"F4.imprint","IMPRINT",FACE,{"disambiguationData":[TD([[makeQuery(id+"F4.imprint","IMPRINT",EDGE,{"disambiguationData":[TD([[subQ2,-1.0]])],"derivedFrom":subQ1}),1.0]])]});}
            var Q8;
            {var subQ1=sQuery(id+"F4.wireOp",EDGE,"E61");var subQ3=sQuery(id+"F4.wireOp",EDGE,"E67");var subQ4=makeQuery(id+"F4.imprint","INTERSECT",VERTEX,{"derivedFrom":[subQ1,subQ3]});Q8=makeQuery(id+"F4.imprint","IMPRINT",FACE,{"disambiguationData":[TD([[makeQuery(id+"F4.imprint","IMPRINT",EDGE,{"disambiguationData":[TD([[subQ4,-1.0]])],"derivedFrom":subQ3}),1.0]])]});}
            var Q9;
            {var subQ1=sQuery(id+"F4.wireOp",EDGE,"E61");var subQ3=sQuery(id+"F4.wireOp",EDGE,"E67");var subQ4=makeQuery(id+"F4.imprint","INTERSECT",VERTEX,{"derivedFrom":[subQ1,subQ3]});Q9=makeQuery(id+"F4.imprint","IMPRINT",FACE,{"disambiguationData":[TD([[makeQuery(id+"F4.imprint","IMPRINT",EDGE,{"disambiguationData":[TD([[subQ4,1.0]])],"derivedFrom":subQ3}),1.0]])]});}
            var Q10;
            {var subQ0=sQuery(id+"F4.wireOp",EDGE,"E73");var subQ1=sQuery(id+"F4.wireOp",EDGE,"E67");var subQ2=makeQuery(id+"F4.imprint","INTERSECT",VERTEX,{"derivedFrom":[subQ1,subQ0]});Q10=makeQuery(id+"F4.imprint","IMPRINT",FACE,{"disambiguationData":[TD([[makeQuery(id+"F4.imprint","IMPRINT",EDGE,{"disambiguationData":[TD([[subQ2,-1.0]])],"derivedFrom":subQ1}),1.0]])]});}
            var Q11;
            {var subQ1=sQuery(id+"F4.wireOp",EDGE,"E65");var subQ3=sQuery(id+"F4.wireOp",EDGE,"E67");var subQ4=makeQuery(id+"F4.imprint","INTERSECT",VERTEX,{"derivedFrom":[subQ1,subQ3]});Q11=makeQuery(id+"F4.imprint","IMPRINT",FACE,{"disambiguationData":[TD([[makeQuery(id+"F4.imprint","IMPRINT",EDGE,{"disambiguationData":[TD([[subQ4,-1.0]])],"derivedFrom":subQ3}),1.0]])]});}
            var Q12;
            {var subQ1=sQuery(id+"F4.wireOp",EDGE,"E65");var subQ3=sQuery(id+"F4.wireOp",EDGE,"E67");var subQ4=makeQuery(id+"F4.imprint","INTERSECT",VERTEX,{"derivedFrom":[subQ1,subQ3]});Q12=makeQuery(id+"F4.imprint","IMPRINT",FACE,{"disambiguationData":[TD([[makeQuery(id+"F4.imprint","IMPRINT",EDGE,{"disambiguationData":[TD([[subQ4,1.0]])],"derivedFrom":subQ3}),1.0]])]});}
            var Q13;
            {var subQ0=sQuery(id+"F4.wireOp",EDGE,"E74");var subQ1=sQuery(id+"F4.wireOp",EDGE,"E67");var subQ2=makeQuery(id+"F4.imprint","INTERSECT",VERTEX,{"derivedFrom":[subQ1,subQ0]});Q13=makeQuery(id+"F4.imprint","IMPRINT",FACE,{"disambiguationData":[TD([[makeQuery(id+"F4.imprint","IMPRINT",EDGE,{"disambiguationData":[TD([[subQ2,1.0]])],"derivedFrom":subQ1}),1.0]])]});}
            var Q14;
            {var subQ1=sQuery(id+"F4.wireOp",EDGE,"E64");var subQ3=sQuery(id+"F4.wireOp",EDGE,"E67");var subQ4=makeQuery(id+"F4.imprint","INTERSECT",VERTEX,{"derivedFrom":[subQ1,subQ3]});Q14=makeQuery(id+"F4.imprint","IMPRINT",FACE,{"disambiguationData":[TD([[makeQuery(id+"F4.imprint","IMPRINT",EDGE,{"disambiguationData":[TD([[subQ4,-1.0]])],"derivedFrom":subQ3}),1.0]])]});}
            var Q15;
            {var subQ1=sQuery(id+"F4.wireOp",EDGE,"E64");var subQ3=sQuery(id+"F4.wireOp",EDGE,"E67");var subQ4=makeQuery(id+"F4.imprint","INTERSECT",VERTEX,{"derivedFrom":[subQ1,subQ3]});Q15=makeQuery(id+"F4.imprint","IMPRINT",FACE,{"disambiguationData":[TD([[makeQuery(id+"F4.imprint","IMPRINT",EDGE,{"disambiguationData":[TD([[subQ4,1.0]])],"derivedFrom":subQ3}),1.0]])]});}
            var Q16;
            {var subQ0=sQuery(id+"F4.wireOp",EDGE,"E77");var subQ1=sQuery(id+"F4.wireOp",EDGE,"E67");var subQ2=makeQuery(id+"F4.imprint","INTERSECT",VERTEX,{"derivedFrom":[subQ1,subQ0]});Q16=makeQuery(id+"F4.imprint","IMPRINT",FACE,{"disambiguationData":[TD([[makeQuery(id+"F4.imprint","IMPRINT",EDGE,{"disambiguationData":[TD([[subQ2,-1.0]])],"derivedFrom":subQ1}),1.0]])]});}
            var Q17;
            {var subQ1=sQuery(id+"F4.wireOp",EDGE,"E63");var subQ3=sQuery(id+"F4.wireOp",EDGE,"E67");var subQ4=makeQuery(id+"F4.imprint","INTERSECT",VERTEX,{"derivedFrom":[subQ1,subQ3]});Q17=makeQuery(id+"F4.imprint","IMPRINT",FACE,{"disambiguationData":[TD([[makeQuery(id+"F4.imprint","IMPRINT",EDGE,{"disambiguationData":[TD([[subQ4,-1.0]])],"derivedFrom":subQ3}),1.0]])]});}
            var Q18;
            {var subQ1=sQuery(id+"F4.wireOp",EDGE,"E63");var subQ3=sQuery(id+"F4.wireOp",EDGE,"E67");var subQ4=makeQuery(id+"F4.imprint","INTERSECT",VERTEX,{"derivedFrom":[subQ1,subQ3]});Q18=makeQuery(id+"F4.imprint","IMPRINT",FACE,{"disambiguationData":[TD([[makeQuery(id+"F4.imprint","IMPRINT",EDGE,{"disambiguationData":[TD([[subQ4,1.0]])],"derivedFrom":subQ3}),1.0]])]});}
            var Q19;
            {var subQ0=sQuery(id+"F4.wireOp",EDGE,"E79");var subQ1=sQuery(id+"F4.wireOp",EDGE,"E67");var subQ2=makeQuery(id+"F4.imprint","INTERSECT",VERTEX,{"derivedFrom":[subQ1,subQ0]});Q19=makeQuery(id+"F4.imprint","IMPRINT",FACE,{"disambiguationData":[TD([[makeQuery(id+"F4.imprint","IMPRINT",EDGE,{"disambiguationData":[TD([[subQ2,-1.0]])],"derivedFrom":subQ1}),1.0]])]});}
            var Q20;
            {var subQ5=sQuery(id+"F4.wireOp",EDGE,"E81");var subQ6=sQuery(id+"F4.wireOp",EDGE,"E66");var subQ7=makeQuery(id+"F4.imprint","INTERSECT",VERTEX,{"derivedFrom":[subQ6,subQ5]});Q20=makeQuery(id+"F4.imprint","IMPRINT",FACE,{"disambiguationData":[TD([[makeQuery(id+"F4.imprint","IMPRINT",EDGE,{"disambiguationData":[TD([[subQ7,-1.0]])],"derivedFrom":subQ6}),-1.0]])]});}
            var Q21;
            {var subQ1=sQuery(id+"F4.wireOp",EDGE,"E66");var subQ5=sQuery(id+"F4.wireOp",EDGE,"E73");var subQ6=makeQuery(id+"F4.imprint","INTERSECT",VERTEX,{"derivedFrom":[subQ1,subQ5]});Q21=makeQuery(id+"F4.imprint","IMPRINT",FACE,{"disambiguationData":[TD([[makeQuery(id+"F4.imprint","IMPRINT",EDGE,{"disambiguationData":[TD([[subQ6,-1.0]])],"derivedFrom":subQ1}),-1.0]])]});}
            var Q22;
            {var subQ1=sQuery(id+"F4.wireOp",EDGE,"E66");var subQ5=sQuery(id+"F4.wireOp",EDGE,"E74");var subQ6=makeQuery(id+"F4.imprint","INTERSECT",VERTEX,{"derivedFrom":[subQ1,subQ5]});Q22=makeQuery(id+"F4.imprint","IMPRINT",FACE,{"disambiguationData":[TD([[makeQuery(id+"F4.imprint","IMPRINT",EDGE,{"disambiguationData":[TD([[subQ6,1.0]])],"derivedFrom":subQ1}),-1.0]])]});}
            var Q23;
            {var subQ0=sQuery(id+"F4.wireOp",EDGE,"E77");var subQ1=sQuery(id+"F4.wireOp",EDGE,"E66");var subQ2=makeQuery(id+"F4.imprint","INTERSECT",VERTEX,{"derivedFrom":[subQ1,subQ0]});Q23=makeQuery(id+"F4.imprint","IMPRINT",FACE,{"disambiguationData":[TD([[makeQuery(id+"F4.imprint","IMPRINT",EDGE,{"disambiguationData":[TD([[subQ2,-1.0]])],"derivedFrom":subQ1}),-1.0]])]});}
            var Q24;
            {var subQ7=sQuery(id+"F4.wireOp",EDGE,"E79");var subQ8=sQuery(id+"F4.wireOp",EDGE,"E66");var subQ9=makeQuery(id+"F4.imprint","INTERSECT",VERTEX,{"derivedFrom":[subQ8,subQ7]});Q24=makeQuery(id+"F4.imprint","IMPRINT",FACE,{"disambiguationData":[TD([[makeQuery(id+"F4.imprint","IMPRINT",EDGE,{"disambiguationData":[TD([[subQ9,-1.0]])],"derivedFrom":subQ8}),-1.0]])]});}
            var Q25;
            {var subQ1=sQuery(id+"F4.wireOp",EDGE,"E60.3");var subQ3=sQuery(id+"F4.wireOp",EDGE,"E72.5");var subQ4=makeQuery(id+"F4.imprint","INTERSECT",VERTEX,{"derivedFrom":[subQ1,subQ3]});Q25=makeQuery(id+"F4.imprint","IMPRINT",FACE,{"disambiguationData":[TD([[makeQuery(id+"F4.imprint","IMPRINT",EDGE,{"disambiguationData":[TD([[subQ4,1.0]])],"derivedFrom":subQ1}),-1.0]])]});}
            var Q26;
            {var subQ1=sQuery(id+"F4.wireOp",EDGE,"E63");var subQ3=sQuery(id+"F4.wireOp",EDGE,"E88");var subQ4=makeQuery(id+"F4.imprint","INTERSECT",VERTEX,{"derivedFrom":[subQ1,subQ3]});Q26=makeQuery(id+"F4.imprint","IMPRINT",FACE,{"disambiguationData":[TD([[makeQuery(id+"F4.imprint","IMPRINT",EDGE,{"disambiguationData":[TD([[subQ4,1.0]])],"derivedFrom":subQ1}),-1.0]])]});}
            var Q27;
            {var subQ1=sQuery(id+"F4.wireOp",EDGE,"E63");var subQ3=sQuery(id+"F4.wireOp",EDGE,"E88");var subQ4=makeQuery(id+"F4.imprint","INTERSECT",VERTEX,{"derivedFrom":[subQ1,subQ3]});Q27=makeQuery(id+"F4.imprint","IMPRINT",FACE,{"disambiguationData":[TD([[makeQuery(id+"F4.imprint","IMPRINT",EDGE,{"disambiguationData":[TD([[subQ4,1.0]])],"derivedFrom":subQ1}),1.0]])]});}
            var Q28;
            {var subQ1=sQuery(id+"F4.wireOp",EDGE,"E60.2");var subQ3=sQuery(id+"F4.wireOp",EDGE,"E72.0");var subQ4=makeQuery(id+"F4.imprint","INTERSECT",VERTEX,{"derivedFrom":[subQ1,subQ3]});Q28=makeQuery(id+"F4.imprint","IMPRINT",FACE,{"disambiguationData":[TD([[makeQuery(id+"F4.imprint","IMPRINT",EDGE,{"disambiguationData":[TD([[subQ4,-1.0]])],"derivedFrom":subQ1}),-1.0]])]});}
            var Q29;
            {var subQ0=sQuery(id+"F4.wireOp",EDGE,"E72.1");Q29=makeQuery(id+"F4.imprint","IMPRINT",FACE,{"disambiguationData":[TD([[makeQuery(id+"F4.imprint","IMPRINT",EDGE,{"derivedFrom":subQ0}),-1.0]])]});}
            var Q30;
            {var subQ0=sQuery(id+"F4.wireOp",EDGE,"E71.1");Q30=makeQuery(id+"F4.imprint","IMPRINT",FACE,{"disambiguationData":[TD([[makeQuery(id+"F4.imprint","IMPRINT",EDGE,{"derivedFrom":subQ0}),-1.0]])]});}
            var Q31;
            {var subQ1=sQuery(id+"F4.wireOp",EDGE,"E60.2");var subQ3=sQuery(id+"F4.wireOp",EDGE,"E71.5");var subQ4=makeQuery(id+"F4.imprint","INTERSECT",VERTEX,{"derivedFrom":[subQ1,subQ3]});Q31=makeQuery(id+"F4.imprint","IMPRINT",FACE,{"disambiguationData":[TD([[makeQuery(id+"F4.imprint","IMPRINT",EDGE,{"disambiguationData":[TD([[subQ4,1.0]])],"derivedFrom":subQ1}),-1.0]])]});}
            var Q32;
            {var subQ1=sQuery(id+"F4.wireOp",EDGE,"E60.1");var subQ3=sQuery(id+"F4.wireOp",EDGE,"E71.0");var subQ4=makeQuery(id+"F4.imprint","INTERSECT",VERTEX,{"derivedFrom":[subQ1,subQ3]});Q32=makeQuery(id+"F4.imprint","IMPRINT",FACE,{"disambiguationData":[TD([[makeQuery(id+"F4.imprint","IMPRINT",EDGE,{"disambiguationData":[TD([[subQ4,-1.0]])],"derivedFrom":subQ1}),-1.0]])]});}
            var Q33;
            {var subQ1=sQuery(id+"F4.wireOp",EDGE,"E64");var subQ3=sQuery(id+"F4.wireOp",EDGE,"E86");var subQ4=makeQuery(id+"F4.imprint","INTERSECT",VERTEX,{"derivedFrom":[subQ1,subQ3]});Q33=makeQuery(id+"F4.imprint","IMPRINT",FACE,{"disambiguationData":[TD([[makeQuery(id+"F4.imprint","IMPRINT",EDGE,{"disambiguationData":[TD([[subQ4,-1.0]])],"derivedFrom":subQ1}),-1.0]])]});}
            var Q34;
            {var subQ1=sQuery(id+"F4.wireOp",EDGE,"E64");var subQ3=sQuery(id+"F4.wireOp",EDGE,"E86");var subQ4=makeQuery(id+"F4.imprint","INTERSECT",VERTEX,{"derivedFrom":[subQ1,subQ3]});Q34=makeQuery(id+"F4.imprint","IMPRINT",FACE,{"disambiguationData":[TD([[makeQuery(id+"F4.imprint","IMPRINT",EDGE,{"disambiguationData":[TD([[subQ4,-1.0]])],"derivedFrom":subQ1}),1.0]])]});}
            var Q35;
            {var subQ0=sQuery(id+"F4.wireOp",EDGE,"E70.1");Q35=makeQuery(id+"F4.imprint","IMPRINT",FACE,{"disambiguationData":[TD([[makeQuery(id+"F4.imprint","IMPRINT",EDGE,{"derivedFrom":subQ0}),-1.0]])]});}
            var Q36;
            {var subQ1=sQuery(id+"F4.wireOp",EDGE,"E60.0");var subQ3=sQuery(id+"F4.wireOp",EDGE,"E70.0");var subQ4=makeQuery(id+"F4.imprint","INTERSECT",VERTEX,{"derivedFrom":[subQ1,subQ3]});Q36=makeQuery(id+"F4.imprint","IMPRINT",FACE,{"disambiguationData":[TD([[makeQuery(id+"F4.imprint","IMPRINT",EDGE,{"disambiguationData":[TD([[subQ4,-1.0]])],"derivedFrom":subQ1}),-1.0]])]});}
            var Q37;
            {var subQ1=sQuery(id+"F4.wireOp",EDGE,"E60.1");var subQ3=sQuery(id+"F4.wireOp",EDGE,"E70.5");var subQ4=makeQuery(id+"F4.imprint","INTERSECT",VERTEX,{"derivedFrom":[subQ1,subQ3]});Q37=makeQuery(id+"F4.imprint","IMPRINT",FACE,{"disambiguationData":[TD([[makeQuery(id+"F4.imprint","IMPRINT",EDGE,{"disambiguationData":[TD([[subQ4,1.0]])],"derivedFrom":subQ1}),-1.0]])]});}
            var Q38;
            {var subQ1=sQuery(id+"F4.wireOp",EDGE,"E65");var subQ3=sQuery(id+"F4.wireOp",EDGE,"E84");var subQ4=makeQuery(id+"F4.imprint","INTERSECT",VERTEX,{"derivedFrom":[subQ1,subQ3]});Q38=makeQuery(id+"F4.imprint","IMPRINT",FACE,{"disambiguationData":[TD([[makeQuery(id+"F4.imprint","IMPRINT",EDGE,{"disambiguationData":[TD([[subQ4,-1.0]])],"derivedFrom":subQ1}),1.0]])]});}
            var Q39;
            {var subQ1=sQuery(id+"F4.wireOp",EDGE,"E65");var subQ3=sQuery(id+"F4.wireOp",EDGE,"E84");var subQ4=makeQuery(id+"F4.imprint","INTERSECT",VERTEX,{"derivedFrom":[subQ1,subQ3]});Q39=makeQuery(id+"F4.imprint","IMPRINT",FACE,{"disambiguationData":[TD([[makeQuery(id+"F4.imprint","IMPRINT",EDGE,{"disambiguationData":[TD([[subQ4,-1.0]])],"derivedFrom":subQ1}),-1.0]])]});}
            var Q40;
            {var subQ0=sQuery(id+"F4.wireOp",EDGE,"E69.1");Q40=makeQuery(id+"F4.imprint","IMPRINT",FACE,{"disambiguationData":[TD([[makeQuery(id+"F4.imprint","IMPRINT",EDGE,{"derivedFrom":subQ0}),-1.0]])]});}
            var Q41;
            {var subQ1=sQuery(id+"F4.wireOp",EDGE,"E60.0");var subQ3=sQuery(id+"F4.wireOp",EDGE,"E69.5");var subQ4=makeQuery(id+"F4.imprint","INTERSECT",VERTEX,{"derivedFrom":[subQ1,subQ3]});Q41=makeQuery(id+"F4.imprint","IMPRINT",FACE,{"disambiguationData":[TD([[makeQuery(id+"F4.imprint","IMPRINT",EDGE,{"disambiguationData":[TD([[subQ4,1.0]])],"derivedFrom":subQ1}),-1.0]])]});}
            var Q42;
            {var subQ1=sQuery(id+"F4.wireOp",EDGE,"E60.4");var subQ3=sQuery(id+"F4.wireOp",EDGE,"E69.0");var subQ4=makeQuery(id+"F4.imprint","INTERSECT",VERTEX,{"derivedFrom":[subQ1,subQ3]});Q42=makeQuery(id+"F4.imprint","IMPRINT",FACE,{"disambiguationData":[TD([[makeQuery(id+"F4.imprint","IMPRINT",EDGE,{"disambiguationData":[TD([[subQ4,-1.0]])],"derivedFrom":subQ1}),-1.0]])]});}
            var Q43;
            {var subQ1=sQuery(id+"F4.wireOp",EDGE,"E61");var subQ3=sQuery(id+"F4.wireOp",EDGE,"E92");var subQ4=makeQuery(id+"F4.imprint","INTERSECT",VERTEX,{"derivedFrom":[subQ1,subQ3]});Q43=makeQuery(id+"F4.imprint","IMPRINT",FACE,{"disambiguationData":[TD([[makeQuery(id+"F4.imprint","IMPRINT",EDGE,{"disambiguationData":[TD([[subQ4,-1.0]])],"derivedFrom":subQ1}),-1.0]])]});}
            var Q44;
            {var subQ1=sQuery(id+"F4.wireOp",EDGE,"E61");var subQ3=sQuery(id+"F4.wireOp",EDGE,"E92");var subQ4=makeQuery(id+"F4.imprint","INTERSECT",VERTEX,{"derivedFrom":[subQ1,subQ3]});Q44=makeQuery(id+"F4.imprint","IMPRINT",FACE,{"disambiguationData":[TD([[makeQuery(id+"F4.imprint","IMPRINT",EDGE,{"disambiguationData":[TD([[subQ4,-1.0]])],"derivedFrom":subQ1}),1.0]])]});}
            extrude(context, id + "F5", {"entities" : qUnion([Q0, Q1, Q2, Q3, Q4, Q5, Q6, Q7, Q8, Q9, Q10, Q11, Q12, Q13, Q14, Q15, Q16, Q17, Q18, Q19, Q20, Q21, Q22, Q23, Q24, Q25, Q26, Q27, Q28, Q29, Q30, Q31, Q32, Q33, Q34, Q35, Q36, Q37, Q38, Q39, Q40, Q41, Q42, Q43, Q44]), "operationType" : NewBodyOperationType.REMOVE, "oppositeDirection" : true, "depth" : 25 * mm, "offsetDistance" : 25 * mm});
        }
        {
            var Q0;
            Q0=makeQuery(id+"F1.opExtrude","CAP_EDGE",EDGE,{"disambiguationData":[OSD([sQuery(id+"F0.wireOp",EDGE,"E54")])],"isStart":false});
            var Q1;
            Q1=makeQuery(id+"F1.opExtrude","CAP_EDGE",EDGE,{"disambiguationData":[OSD([sQuery(id+"F0.wireOp",EDGE,"E54")])],"isStart":true});
            var Q2;
            Q2=makeQuery(id+"F1.opExtrude","CAP_EDGE",EDGE,{"disambiguationData":[OSD([sQuery(id+"F0.wireOp",EDGE,"E42")])],"isStart":false});
            var Q3;
            Q3=makeQuery(id+"F1.opExtrude","CAP_EDGE",EDGE,{"disambiguationData":[OSD([sQuery(id+"F0.wireOp",EDGE,"E43")])],"isStart":false});
            var Q4;
            Q4=makeQuery(id+"F1.opExtrude","CAP_EDGE",EDGE,{"disambiguationData":[OSD([sQuery(id+"F0.wireOp",EDGE,"E44")])],"isStart":false});
            var Q5;
            Q5=makeQuery(id+"F1.opExtrude","CAP_EDGE",EDGE,{"disambiguationData":[OSD([sQuery(id+"F0.wireOp",EDGE,"E45")])],"isStart":false});
            var Q6;
            Q6=makeQuery(id+"F1.opExtrude","CAP_EDGE",EDGE,{"disambiguationData":[OSD([sQuery(id+"F0.wireOp",EDGE,"E41")])],"isStart":false});
            var Q7;
            Q7=makeQuery(id+"F1.opExtrude","CAP_EDGE",EDGE,{"disambiguationData":[OSD([sQuery(id+"F0.wireOp",EDGE,"E41")])],"isStart":true});
            var Q8;
            Q8=makeQuery(id+"F1.opExtrude","CAP_EDGE",EDGE,{"disambiguationData":[OSD([sQuery(id+"F0.wireOp",EDGE,"E45")])],"isStart":true});
            var Q9;
            Q9=makeQuery(id+"F1.opExtrude","CAP_EDGE",EDGE,{"disambiguationData":[OSD([sQuery(id+"F0.wireOp",EDGE,"E43")])],"isStart":true});
            var Q10;
            Q10=makeQuery(id+"F1.opExtrude","CAP_EDGE",EDGE,{"disambiguationData":[OSD([sQuery(id+"F0.wireOp",EDGE,"E44")])],"isStart":true});
            var Q11;
            Q11=makeQuery(id+"F1.opExtrude","CAP_EDGE",EDGE,{"disambiguationData":[OSD([sQuery(id+"F0.wireOp",EDGE,"E42")])],"isStart":true});
            fillet(context, id + "F6", {"entities" : qUnion([Q0, Q1, Q2, Q3, Q4, Q5, Q6, Q7, Q8, Q9, Q10, Q11]), "radius" : 2 * mm, "tangentPropagation" : true, "allowEdgeOverflow" : false});
        }
        {
            var Q0;
            Q0=makeQuery(id+"F2.opExtrude","CAP_EDGE",EDGE,{"disambiguationData":[OSD([sQuery(id+"F0.wireOp",EDGE,"E56")])],"isStart":false});
            var Q1;
            Q1=makeQuery(id+"F2.opExtrude","CAP_EDGE",EDGE,{"disambiguationData":[OSD([sQuery(id+"F0.wireOp",EDGE,"E56")])],"isStart":true});
            var Q2;
            Q2=makeQuery(id+"F2.opExtrude","CAP_EDGE",EDGE,{"disambiguationData":[OSD([sQuery(id+"F0.wireOp",EDGE,"E55")])],"isStart":false});
            var Q3;
            Q3=makeQuery(id+"F2.opExtrude","CAP_EDGE",EDGE,{"disambiguationData":[OSD([sQuery(id+"F0.wireOp",EDGE,"E55")])],"isStart":true});
            var Q4;
            Q4=makeQuery(id+"F2.opExtrude","CAP_EDGE",EDGE,{"disambiguationData":[OSD([sQuery(id+"F0.wireOp",EDGE,"E59")])],"isStart":false});
            var Q5;
            Q5=makeQuery(id+"F2.opExtrude","CAP_EDGE",EDGE,{"disambiguationData":[OSD([sQuery(id+"F0.wireOp",EDGE,"E59")])],"isStart":true});
            var Q6;
            Q6=makeQuery(id+"F2.opExtrude","CAP_EDGE",EDGE,{"disambiguationData":[OSD([sQuery(id+"F0.wireOp",EDGE,"E58")])],"isStart":false});
            var Q7;
            Q7=makeQuery(id+"F2.opExtrude","CAP_EDGE",EDGE,{"disambiguationData":[OSD([sQuery(id+"F0.wireOp",EDGE,"E58")])],"isStart":true});
            var Q8;
            Q8=makeQuery(id+"F2.opExtrude","CAP_EDGE",EDGE,{"disambiguationData":[OSD([sQuery(id+"F0.wireOp",EDGE,"E57")])],"isStart":true});
            var Q9;
            Q9=makeQuery(id+"F2.opExtrude","CAP_EDGE",EDGE,{"disambiguationData":[OSD([sQuery(id+"F0.wireOp",EDGE,"E57")])],"isStart":false});
            fillet(context, id + "F7", {"entities" : qUnion([Q0, Q1, Q2, Q3, Q4, Q5, Q6, Q7, Q8, Q9]), "radius" : 2 * mm, "tangentPropagation" : true, "allowEdgeOverflow" : false});
        }
        {
            var Q0;
            Q0=makeQuery(id+"F5.boolean.opBoolean","COPY",EDGE,{"derivedFrom":makeQuery(id+"F5.opExtrude","SWEPT_EDGE",EDGE,{"disambiguationData":[OSD([sQuery(id+"F4.wireOp",EDGE,"E66"),sQuery(id+"F4.wireOp",EDGE,"E79")])]})});
            var Q1;
            Q1=makeQuery(id+"F5.boolean.opBoolean","COPY",EDGE,{"derivedFrom":makeQuery(id+"F5.opExtrude","SWEPT_EDGE",EDGE,{"disambiguationData":[OSD([sQuery(id+"F4.wireOp",EDGE,"E66"),sQuery(id+"F4.wireOp",EDGE,"E76")])]})});
            var Q2;
            Q2=makeQuery(id+"F5.boolean.opBoolean","COPY",EDGE,{"derivedFrom":makeQuery(id+"F5.opExtrude","SWEPT_EDGE",EDGE,{"disambiguationData":[OSD([sQuery(id+"F4.wireOp",EDGE,"E66"),sQuery(id+"F4.wireOp",EDGE,"E78")])]})});
            var Q3;
            Q3=makeQuery(id+"F5.boolean.opBoolean","COPY",EDGE,{"derivedFrom":makeQuery(id+"F5.opExtrude","SWEPT_EDGE",EDGE,{"disambiguationData":[OSD([sQuery(id+"F4.wireOp",EDGE,"E66"),sQuery(id+"F4.wireOp",EDGE,"E77")])]})});
            var Q4;
            Q4=makeQuery(id+"F5.boolean.opBoolean","COPY",EDGE,{"derivedFrom":makeQuery(id+"F5.opExtrude","SWEPT_EDGE",EDGE,{"disambiguationData":[OSD([sQuery(id+"F4.wireOp",EDGE,"E66"),sQuery(id+"F4.wireOp",EDGE,"E74")])]})});
            var Q5;
            Q5=makeQuery(id+"F5.boolean.opBoolean","COPY",EDGE,{"derivedFrom":makeQuery(id+"F5.opExtrude","SWEPT_EDGE",EDGE,{"disambiguationData":[OSD([sQuery(id+"F4.wireOp",EDGE,"E66"),sQuery(id+"F4.wireOp",EDGE,"E75")])]})});
            var Q6;
            Q6=makeQuery(id+"F5.boolean.opBoolean","COPY",EDGE,{"derivedFrom":makeQuery(id+"F5.opExtrude","SWEPT_EDGE",EDGE,{"disambiguationData":[OSD([sQuery(id+"F4.wireOp",EDGE,"E66"),sQuery(id+"F4.wireOp",EDGE,"E82")])]})});
            var Q7;
            Q7=makeQuery(id+"F5.boolean.opBoolean","COPY",EDGE,{"derivedFrom":makeQuery(id+"F5.opExtrude","SWEPT_EDGE",EDGE,{"disambiguationData":[OSD([sQuery(id+"F4.wireOp",EDGE,"E66"),sQuery(id+"F4.wireOp",EDGE,"E73")])]})});
            var Q8;
            Q8=makeQuery(id+"F5.boolean.opBoolean","COPY",EDGE,{"derivedFrom":makeQuery(id+"F5.opExtrude","SWEPT_EDGE",EDGE,{"disambiguationData":[OSD([sQuery(id+"F4.wireOp",EDGE,"E66"),sQuery(id+"F4.wireOp",EDGE,"E81")])]})});
            var Q9;
            Q9=makeQuery(id+"F5.boolean.opBoolean","COPY",EDGE,{"derivedFrom":makeQuery(id+"F5.opExtrude","SWEPT_EDGE",EDGE,{"disambiguationData":[OSD([sQuery(id+"F4.wireOp",EDGE,"E66"),sQuery(id+"F4.wireOp",EDGE,"E80")])]})});
            fillet(context, id + "F8", {"entities" : qUnion([Q0, Q1, Q2, Q3, Q4, Q5, Q6, Q7, Q8, Q9]), "radius" : 3 * mm, "tangentPropagation" : true, "allowEdgeOverflow" : false});
        }
        {
            var Q0;
            Q0=makeQuery(id+"F5.boolean.opBoolean","COPY",EDGE,{"derivedFrom":makeQuery(id+"F5.opExtrude","CAP_EDGE",EDGE,{"disambiguationData":[OSD([sQuery(id+"F4.wireOp",EDGE,"E67")])],"isStart":true})});
            var Q1;
            Q1=makeQuery(id+"F5.boolean.opBoolean","COPY",EDGE,{"derivedFrom":makeQuery(id+"F5.opExtrude","CAP_EDGE",EDGE,{"disambiguationData":[OSD([sQuery(id+"F4.wireOp",EDGE,"E69.2")])],"isStart":true})});
            var Q2;
            Q2=makeQuery(id+"F5.boolean.opBoolean","COPY",EDGE,{"derivedFrom":makeQuery(id+"F5.opExtrude","CAP_EDGE",EDGE,{"disambiguationData":[OSD([sQuery(id+"F4.wireOp",EDGE,"E69.1")])],"isStart":true})});
            var Q3;
            Q3=makeQuery(id+"F5.boolean.opBoolean","COPY",EDGE,{"derivedFrom":makeQuery(id+"F5.opExtrude","CAP_EDGE",EDGE,{"disambiguationData":[OSD([sQuery(id+"F4.wireOp",EDGE,"E69.3")])],"isStart":true})});
            var Q4;
            Q4=makeQuery(id+"F5.boolean.opBoolean","COPY",EDGE,{"derivedFrom":makeQuery(id+"F5.opExtrude","CAP_EDGE",EDGE,{"disambiguationData":[OSD([sQuery(id+"F4.wireOp",EDGE,"E69.4")])],"isStart":true})});
            var Q5;
            Q5=makeQuery(id+"F5.boolean.opBoolean","COPY",EDGE,{"derivedFrom":makeQuery(id+"F5.opExtrude","CAP_EDGE",EDGE,{"disambiguationData":[OSD([sQuery(id+"F4.wireOp",EDGE,"E69.5")])],"isStart":true})});
            var Q6;
            Q6=makeQuery(id+"F5.boolean.opBoolean","COPY",EDGE,{"derivedFrom":makeQuery(id+"F5.opExtrude","CAP_EDGE",EDGE,{"disambiguationData":[OSD([sQuery(id+"F4.wireOp",EDGE,"E69.0")])],"isStart":true})});
            var Q7;
            Q7=makeQuery(id+"F5.boolean.opBoolean","COPY",EDGE,{"derivedFrom":makeQuery(id+"F5.opExtrude","CAP_EDGE",EDGE,{"disambiguationData":[OSD([sQuery(id+"F4.wireOp",EDGE,"E68.4")])],"isStart":true})});
            var Q8;
            Q8=makeQuery(id+"F5.boolean.opBoolean","COPY",EDGE,{"derivedFrom":makeQuery(id+"F5.opExtrude","CAP_EDGE",EDGE,{"disambiguationData":[OSD([sQuery(id+"F4.wireOp",EDGE,"E68.3")])],"isStart":true})});
            var Q9;
            Q9=makeQuery(id+"F5.boolean.opBoolean","COPY",EDGE,{"derivedFrom":makeQuery(id+"F5.opExtrude","CAP_EDGE",EDGE,{"disambiguationData":[OSD([sQuery(id+"F4.wireOp",EDGE,"E68.2")])],"isStart":true})});
            var Q10;
            Q10=makeQuery(id+"F5.boolean.opBoolean","COPY",EDGE,{"derivedFrom":makeQuery(id+"F5.opExtrude","CAP_EDGE",EDGE,{"disambiguationData":[OSD([sQuery(id+"F4.wireOp",EDGE,"E68.1")])],"isStart":true})});
            var Q11;
            Q11=makeQuery(id+"F5.boolean.opBoolean","COPY",EDGE,{"derivedFrom":makeQuery(id+"F5.opExtrude","CAP_EDGE",EDGE,{"disambiguationData":[OSD([sQuery(id+"F4.wireOp",EDGE,"E68.0")])],"isStart":true})});
            var Q12;
            Q12=makeQuery(id+"F5.boolean.opBoolean","COPY",EDGE,{"derivedFrom":makeQuery(id+"F5.opExtrude","CAP_EDGE",EDGE,{"disambiguationData":[OSD([sQuery(id+"F4.wireOp",EDGE,"E68.5")])],"isStart":true})});
            var Q13;
            Q13=makeQuery(id+"F5.boolean.opBoolean","COPY",EDGE,{"derivedFrom":makeQuery(id+"F5.opExtrude","CAP_EDGE",EDGE,{"disambiguationData":[OSD([sQuery(id+"F4.wireOp",EDGE,"E72.5")])],"isStart":true})});
            var Q14;
            Q14=makeQuery(id+"F5.boolean.opBoolean","COPY",EDGE,{"derivedFrom":makeQuery(id+"F5.opExtrude","CAP_EDGE",EDGE,{"disambiguationData":[OSD([sQuery(id+"F4.wireOp",EDGE,"E72.4")])],"isStart":true})});
            var Q15;
            Q15=makeQuery(id+"F5.boolean.opBoolean","COPY",EDGE,{"derivedFrom":makeQuery(id+"F5.opExtrude","CAP_EDGE",EDGE,{"disambiguationData":[OSD([sQuery(id+"F4.wireOp",EDGE,"E72.3")])],"isStart":true})});
            var Q16;
            Q16=makeQuery(id+"F5.boolean.opBoolean","COPY",EDGE,{"derivedFrom":makeQuery(id+"F5.opExtrude","CAP_EDGE",EDGE,{"disambiguationData":[OSD([sQuery(id+"F4.wireOp",EDGE,"E72.2")])],"isStart":true})});
            var Q17;
            Q17=makeQuery(id+"F5.boolean.opBoolean","COPY",EDGE,{"derivedFrom":makeQuery(id+"F5.opExtrude","CAP_EDGE",EDGE,{"disambiguationData":[OSD([sQuery(id+"F4.wireOp",EDGE,"E72.1")])],"isStart":true})});
            var Q18;
            Q18=makeQuery(id+"F5.boolean.opBoolean","COPY",EDGE,{"derivedFrom":makeQuery(id+"F5.opExtrude","CAP_EDGE",EDGE,{"disambiguationData":[OSD([sQuery(id+"F4.wireOp",EDGE,"E72.0")])],"isStart":true})});
            var Q19;
            Q19=makeQuery(id+"F5.boolean.opBoolean","COPY",EDGE,{"derivedFrom":makeQuery(id+"F5.opExtrude","CAP_EDGE",EDGE,{"disambiguationData":[OSD([sQuery(id+"F4.wireOp",EDGE,"E71.0")])],"isStart":true})});
            var Q20;
            Q20=makeQuery(id+"F5.boolean.opBoolean","COPY",EDGE,{"derivedFrom":makeQuery(id+"F5.opExtrude","CAP_EDGE",EDGE,{"disambiguationData":[OSD([sQuery(id+"F4.wireOp",EDGE,"E71.5")])],"isStart":true})});
            var Q21;
            Q21=makeQuery(id+"F5.boolean.opBoolean","COPY",EDGE,{"derivedFrom":makeQuery(id+"F5.opExtrude","CAP_EDGE",EDGE,{"disambiguationData":[OSD([sQuery(id+"F4.wireOp",EDGE,"E71.4")])],"isStart":true})});
            var Q22;
            Q22=makeQuery(id+"F5.boolean.opBoolean","COPY",EDGE,{"derivedFrom":makeQuery(id+"F5.opExtrude","CAP_EDGE",EDGE,{"disambiguationData":[OSD([sQuery(id+"F4.wireOp",EDGE,"E71.3")])],"isStart":true})});
            var Q23;
            Q23=makeQuery(id+"F5.boolean.opBoolean","COPY",EDGE,{"derivedFrom":makeQuery(id+"F5.opExtrude","CAP_EDGE",EDGE,{"disambiguationData":[OSD([sQuery(id+"F4.wireOp",EDGE,"E71.2")])],"isStart":true})});
            var Q24;
            Q24=makeQuery(id+"F5.boolean.opBoolean","COPY",EDGE,{"derivedFrom":makeQuery(id+"F5.opExtrude","CAP_EDGE",EDGE,{"disambiguationData":[OSD([sQuery(id+"F4.wireOp",EDGE,"E71.1")])],"isStart":true})});
            var Q25;
            Q25=makeQuery(id+"F5.boolean.opBoolean","COPY",EDGE,{"derivedFrom":makeQuery(id+"F5.opExtrude","CAP_EDGE",EDGE,{"disambiguationData":[OSD([sQuery(id+"F4.wireOp",EDGE,"E70.0")])],"isStart":true})});
            var Q26;
            Q26=makeQuery(id+"F5.boolean.opBoolean","COPY",EDGE,{"derivedFrom":makeQuery(id+"F5.opExtrude","CAP_EDGE",EDGE,{"disambiguationData":[OSD([sQuery(id+"F4.wireOp",EDGE,"E70.1")])],"isStart":true})});
            var Q27;
            Q27=makeQuery(id+"F5.boolean.opBoolean","COPY",EDGE,{"derivedFrom":makeQuery(id+"F5.opExtrude","CAP_EDGE",EDGE,{"disambiguationData":[OSD([sQuery(id+"F4.wireOp",EDGE,"E70.2")])],"isStart":true})});
            var Q28;
            Q28=makeQuery(id+"F5.boolean.opBoolean","COPY",EDGE,{"derivedFrom":makeQuery(id+"F5.opExtrude","CAP_EDGE",EDGE,{"disambiguationData":[OSD([sQuery(id+"F4.wireOp",EDGE,"E70.4")])],"isStart":true})});
            var Q29;
            Q29=makeQuery(id+"F5.boolean.opBoolean","COPY",EDGE,{"derivedFrom":makeQuery(id+"F5.opExtrude","CAP_EDGE",EDGE,{"disambiguationData":[OSD([sQuery(id+"F4.wireOp",EDGE,"E70.5")])],"isStart":true})});
            var Q30;
            Q30=makeQuery(id+"F5.boolean.opBoolean","COPY",EDGE,{"derivedFrom":makeQuery(id+"F5.opExtrude","CAP_EDGE",EDGE,{"disambiguationData":[OSD([sQuery(id+"F4.wireOp",EDGE,"E70.3")])],"isStart":true})});
            var Q31;
            Q31=makeQuery(id+"F5.boolean.opBoolean","INTERSECT",EDGE,{"derivedFrom":[makeQuery(id+"F2.opExtrude","CAP_FACE",FACE,{"disambiguationData":[OSD([sQuery(id+"F0.wireOp",EDGE,"E41"),sQuery(id+"F0.wireOp",EDGE,"E42"),sQuery(id+"F0.wireOp",EDGE,"E43"),sQuery(id+"F0.wireOp",EDGE,"E44"),sQuery(id+"F0.wireOp",EDGE,"E45"),sQuery(id+"F0.wireOp",EDGE,"E54"),sQuery(id+"F0.wireOp",EDGE,"E55"),sQuery(id+"F0.wireOp",EDGE,"E56"),sQuery(id+"F0.wireOp",EDGE,"E57"),sQuery(id+"F0.wireOp",EDGE,"E58"),sQuery(id+"F0.wireOp",EDGE,"E59")])],"isStart":false}),makeQuery(id+"F5.opExtrude","SWEPT_FACE",FACE,{"disambiguationData":[OSD([sQuery(id+"F4.wireOp",EDGE,"E91")])]})]});
            var Q32;
            Q32=makeQuery(id+"F5.boolean.opBoolean","INTERSECT",EDGE,{"derivedFrom":[makeQuery(id+"F2.opExtrude","CAP_FACE",FACE,{"disambiguationData":[OSD([sQuery(id+"F0.wireOp",EDGE,"E41"),sQuery(id+"F0.wireOp",EDGE,"E42"),sQuery(id+"F0.wireOp",EDGE,"E43"),sQuery(id+"F0.wireOp",EDGE,"E44"),sQuery(id+"F0.wireOp",EDGE,"E45"),sQuery(id+"F0.wireOp",EDGE,"E54"),sQuery(id+"F0.wireOp",EDGE,"E55"),sQuery(id+"F0.wireOp",EDGE,"E56"),sQuery(id+"F0.wireOp",EDGE,"E57"),sQuery(id+"F0.wireOp",EDGE,"E58"),sQuery(id+"F0.wireOp",EDGE,"E59")])],"isStart":false}),makeQuery(id+"F5.opExtrude","SWEPT_FACE",FACE,{"disambiguationData":[OSD([sQuery(id+"F4.wireOp",EDGE,"E83")])]})]});
            var Q33;
            Q33=makeQuery(id+"F5.boolean.opBoolean","INTERSECT",EDGE,{"derivedFrom":[makeQuery(id+"F2.opExtrude","CAP_FACE",FACE,{"disambiguationData":[OSD([sQuery(id+"F0.wireOp",EDGE,"E41"),sQuery(id+"F0.wireOp",EDGE,"E42"),sQuery(id+"F0.wireOp",EDGE,"E43"),sQuery(id+"F0.wireOp",EDGE,"E44"),sQuery(id+"F0.wireOp",EDGE,"E45"),sQuery(id+"F0.wireOp",EDGE,"E54"),sQuery(id+"F0.wireOp",EDGE,"E55"),sQuery(id+"F0.wireOp",EDGE,"E56"),sQuery(id+"F0.wireOp",EDGE,"E57"),sQuery(id+"F0.wireOp",EDGE,"E58"),sQuery(id+"F0.wireOp",EDGE,"E59")])],"isStart":false}),makeQuery(id+"F5.opExtrude","SWEPT_FACE",FACE,{"disambiguationData":[OSD([sQuery(id+"F4.wireOp",EDGE,"E89")])]})]});
            var Q34;
            Q34=makeQuery(id+"F5.boolean.opBoolean","INTERSECT",EDGE,{"derivedFrom":[makeQuery(id+"F2.opExtrude","CAP_FACE",FACE,{"disambiguationData":[OSD([sQuery(id+"F0.wireOp",EDGE,"E41"),sQuery(id+"F0.wireOp",EDGE,"E42"),sQuery(id+"F0.wireOp",EDGE,"E43"),sQuery(id+"F0.wireOp",EDGE,"E44"),sQuery(id+"F0.wireOp",EDGE,"E45"),sQuery(id+"F0.wireOp",EDGE,"E54"),sQuery(id+"F0.wireOp",EDGE,"E55"),sQuery(id+"F0.wireOp",EDGE,"E56"),sQuery(id+"F0.wireOp",EDGE,"E57"),sQuery(id+"F0.wireOp",EDGE,"E58"),sQuery(id+"F0.wireOp",EDGE,"E59")])],"isStart":false}),makeQuery(id+"F5.opExtrude","SWEPT_FACE",FACE,{"disambiguationData":[OSD([sQuery(id+"F4.wireOp",EDGE,"E87")])]})]});
            var Q35;
            Q35=makeQuery(id+"F5.boolean.opBoolean","INTERSECT",EDGE,{"derivedFrom":[makeQuery(id+"F2.opExtrude","CAP_FACE",FACE,{"disambiguationData":[OSD([sQuery(id+"F0.wireOp",EDGE,"E41"),sQuery(id+"F0.wireOp",EDGE,"E42"),sQuery(id+"F0.wireOp",EDGE,"E43"),sQuery(id+"F0.wireOp",EDGE,"E44"),sQuery(id+"F0.wireOp",EDGE,"E45"),sQuery(id+"F0.wireOp",EDGE,"E54"),sQuery(id+"F0.wireOp",EDGE,"E55"),sQuery(id+"F0.wireOp",EDGE,"E56"),sQuery(id+"F0.wireOp",EDGE,"E57"),sQuery(id+"F0.wireOp",EDGE,"E58"),sQuery(id+"F0.wireOp",EDGE,"E59")])],"isStart":false}),makeQuery(id+"F5.opExtrude","SWEPT_FACE",FACE,{"disambiguationData":[OSD([sQuery(id+"F4.wireOp",EDGE,"E85")])]})]});
            chamfer(context, id + "F9", {"entities" : qUnion([Q0, Q1, Q2, Q3, Q4, Q5, Q6, Q7, Q8, Q9, Q10, Q11, Q12, Q13, Q14, Q15, Q16, Q17, Q18, Q19, Q20, Q21, Q22, Q23, Q24, Q25, Q26, Q27, Q28, Q29, Q30, Q31, Q32, Q33, Q34, Q35]), "width" : 1 * mm, "tangentPropagation" : true});
        }
        {
            var Q0;
            Q0=makeQuery(id+"F5.boolean.opBoolean","INTERSECT",EDGE,{"derivedFrom":[makeQuery(id+"F1.opExtrude","CAP_FACE",FACE,{"disambiguationData":[OSD([sQuery(id+"F0.wireOp",EDGE,"E43")])],"isStart":true}),makeQuery(id+"F5.opExtrude","SWEPT_FACE",FACE,{"disambiguationData":[OSD([sQuery(id+"F4.wireOp",EDGE,"E69.5")])]})]});
            var Q1;
            Q1=makeQuery(id+"F5.boolean.opBoolean","INTERSECT",EDGE,{"derivedFrom":[makeQuery(id+"F1.opExtrude","CAP_FACE",FACE,{"disambiguationData":[OSD([sQuery(id+"F0.wireOp",EDGE,"E43")])],"isStart":true}),makeQuery(id+"F5.opExtrude","SWEPT_FACE",FACE,{"disambiguationData":[OSD([sQuery(id+"F4.wireOp",EDGE,"E69.4")])]})]});
            var Q2;
            Q2=makeQuery(id+"F5.boolean.opBoolean","INTERSECT",EDGE,{"derivedFrom":[makeQuery(id+"F1.opExtrude","CAP_FACE",FACE,{"disambiguationData":[OSD([sQuery(id+"F0.wireOp",EDGE,"E43")])],"isStart":true}),makeQuery(id+"F5.opExtrude","SWEPT_FACE",FACE,{"disambiguationData":[OSD([sQuery(id+"F4.wireOp",EDGE,"E69.3")])]})]});
            var Q3;
            Q3=makeQuery(id+"F5.boolean.opBoolean","INTERSECT",EDGE,{"derivedFrom":[makeQuery(id+"F1.opExtrude","CAP_FACE",FACE,{"disambiguationData":[OSD([sQuery(id+"F0.wireOp",EDGE,"E43")])],"isStart":true}),makeQuery(id+"F5.opExtrude","SWEPT_FACE",FACE,{"disambiguationData":[OSD([sQuery(id+"F4.wireOp",EDGE,"E69.2")])]})]});
            var Q4;
            Q4=makeQuery(id+"F5.boolean.opBoolean","INTERSECT",EDGE,{"derivedFrom":[makeQuery(id+"F1.opExtrude","CAP_FACE",FACE,{"disambiguationData":[OSD([sQuery(id+"F0.wireOp",EDGE,"E43")])],"isStart":true}),makeQuery(id+"F5.opExtrude","SWEPT_FACE",FACE,{"disambiguationData":[OSD([sQuery(id+"F4.wireOp",EDGE,"E69.1")])]})]});
            var Q5;
            Q5=makeQuery(id+"F5.boolean.opBoolean","INTERSECT",EDGE,{"derivedFrom":[makeQuery(id+"F1.opExtrude","CAP_FACE",FACE,{"disambiguationData":[OSD([sQuery(id+"F0.wireOp",EDGE,"E43")])],"isStart":true}),makeQuery(id+"F5.opExtrude","SWEPT_FACE",FACE,{"disambiguationData":[OSD([sQuery(id+"F4.wireOp",EDGE,"E69.0")])]})]});
            var Q6;
            Q6=makeQuery(id+"F5.boolean.opBoolean","INTERSECT",EDGE,{"derivedFrom":[makeQuery(id+"F1.opExtrude","CAP_FACE",FACE,{"disambiguationData":[OSD([sQuery(id+"F0.wireOp",EDGE,"E42")])],"isStart":true}),makeQuery(id+"F5.opExtrude","SWEPT_FACE",FACE,{"disambiguationData":[OSD([sQuery(id+"F4.wireOp",EDGE,"E68.5")])]})]});
            var Q7;
            Q7=makeQuery(id+"F5.boolean.opBoolean","INTERSECT",EDGE,{"derivedFrom":[makeQuery(id+"F1.opExtrude","CAP_FACE",FACE,{"disambiguationData":[OSD([sQuery(id+"F0.wireOp",EDGE,"E42")])],"isStart":true}),makeQuery(id+"F5.opExtrude","SWEPT_FACE",FACE,{"disambiguationData":[OSD([sQuery(id+"F4.wireOp",EDGE,"E68.0")])]})]});
            var Q8;
            Q8=makeQuery(id+"F5.boolean.opBoolean","INTERSECT",EDGE,{"derivedFrom":[makeQuery(id+"F1.opExtrude","CAP_FACE",FACE,{"disambiguationData":[OSD([sQuery(id+"F0.wireOp",EDGE,"E42")])],"isStart":true}),makeQuery(id+"F5.opExtrude","SWEPT_FACE",FACE,{"disambiguationData":[OSD([sQuery(id+"F4.wireOp",EDGE,"E68.1")])]})]});
            var Q9;
            Q9=makeQuery(id+"F5.boolean.opBoolean","INTERSECT",EDGE,{"derivedFrom":[makeQuery(id+"F1.opExtrude","CAP_FACE",FACE,{"disambiguationData":[OSD([sQuery(id+"F0.wireOp",EDGE,"E42")])],"isStart":true}),makeQuery(id+"F5.opExtrude","SWEPT_FACE",FACE,{"disambiguationData":[OSD([sQuery(id+"F4.wireOp",EDGE,"E68.2")])]})]});
            var Q10;
            Q10=makeQuery(id+"F5.boolean.opBoolean","INTERSECT",EDGE,{"derivedFrom":[makeQuery(id+"F1.opExtrude","CAP_FACE",FACE,{"disambiguationData":[OSD([sQuery(id+"F0.wireOp",EDGE,"E42")])],"isStart":true}),makeQuery(id+"F5.opExtrude","SWEPT_FACE",FACE,{"disambiguationData":[OSD([sQuery(id+"F4.wireOp",EDGE,"E68.3")])]})]});
            var Q11;
            Q11=makeQuery(id+"F5.boolean.opBoolean","INTERSECT",EDGE,{"derivedFrom":[makeQuery(id+"F1.opExtrude","CAP_FACE",FACE,{"disambiguationData":[OSD([sQuery(id+"F0.wireOp",EDGE,"E41")])],"isStart":true}),makeQuery(id+"F5.opExtrude","SWEPT_FACE",FACE,{"disambiguationData":[OSD([sQuery(id+"F4.wireOp",EDGE,"E72.0")])]})]});
            var Q12;
            Q12=makeQuery(id+"F5.boolean.opBoolean","INTERSECT",EDGE,{"derivedFrom":[makeQuery(id+"F1.opExtrude","CAP_FACE",FACE,{"disambiguationData":[OSD([sQuery(id+"F0.wireOp",EDGE,"E41")])],"isStart":true}),makeQuery(id+"F5.opExtrude","SWEPT_FACE",FACE,{"disambiguationData":[OSD([sQuery(id+"F4.wireOp",EDGE,"E72.1")])]})]});
            var Q13;
            Q13=makeQuery(id+"F5.boolean.opBoolean","INTERSECT",EDGE,{"derivedFrom":[makeQuery(id+"F1.opExtrude","CAP_FACE",FACE,{"disambiguationData":[OSD([sQuery(id+"F0.wireOp",EDGE,"E41")])],"isStart":true}),makeQuery(id+"F5.opExtrude","SWEPT_FACE",FACE,{"disambiguationData":[OSD([sQuery(id+"F4.wireOp",EDGE,"E72.2")])]})]});
            var Q14;
            Q14=makeQuery(id+"F5.boolean.opBoolean","INTERSECT",EDGE,{"derivedFrom":[makeQuery(id+"F1.opExtrude","CAP_FACE",FACE,{"disambiguationData":[OSD([sQuery(id+"F0.wireOp",EDGE,"E41")])],"isStart":true}),makeQuery(id+"F5.opExtrude","SWEPT_FACE",FACE,{"disambiguationData":[OSD([sQuery(id+"F4.wireOp",EDGE,"E72.5")])]})]});
            var Q15;
            Q15=makeQuery(id+"F5.boolean.opBoolean","INTERSECT",EDGE,{"derivedFrom":[makeQuery(id+"F1.opExtrude","CAP_FACE",FACE,{"disambiguationData":[OSD([sQuery(id+"F0.wireOp",EDGE,"E41")])],"isStart":true}),makeQuery(id+"F5.opExtrude","SWEPT_FACE",FACE,{"disambiguationData":[OSD([sQuery(id+"F4.wireOp",EDGE,"E72.4")])]})]});
            var Q16;
            Q16=makeQuery(id+"F5.boolean.opBoolean","INTERSECT",EDGE,{"derivedFrom":[makeQuery(id+"F1.opExtrude","CAP_FACE",FACE,{"disambiguationData":[OSD([sQuery(id+"F0.wireOp",EDGE,"E41")])],"isStart":true}),makeQuery(id+"F5.opExtrude","SWEPT_FACE",FACE,{"disambiguationData":[OSD([sQuery(id+"F4.wireOp",EDGE,"E72.3")])]})]});
            var Q17;
            Q17=makeQuery(id+"F5.boolean.opBoolean","INTERSECT",EDGE,{"derivedFrom":[makeQuery(id+"F1.opExtrude","CAP_FACE",FACE,{"disambiguationData":[OSD([sQuery(id+"F0.wireOp",EDGE,"E45")])],"isStart":true}),makeQuery(id+"F5.opExtrude","SWEPT_FACE",FACE,{"disambiguationData":[OSD([sQuery(id+"F4.wireOp",EDGE,"E71.2")])]})]});
            var Q18;
            Q18=makeQuery(id+"F5.boolean.opBoolean","INTERSECT",EDGE,{"derivedFrom":[makeQuery(id+"F1.opExtrude","CAP_FACE",FACE,{"disambiguationData":[OSD([sQuery(id+"F0.wireOp",EDGE,"E45")])],"isStart":true}),makeQuery(id+"F5.opExtrude","SWEPT_FACE",FACE,{"disambiguationData":[OSD([sQuery(id+"F4.wireOp",EDGE,"E71.3")])]})]});
            var Q19;
            Q19=makeQuery(id+"F5.boolean.opBoolean","INTERSECT",EDGE,{"derivedFrom":[makeQuery(id+"F1.opExtrude","CAP_FACE",FACE,{"disambiguationData":[OSD([sQuery(id+"F0.wireOp",EDGE,"E45")])],"isStart":true}),makeQuery(id+"F5.opExtrude","SWEPT_FACE",FACE,{"disambiguationData":[OSD([sQuery(id+"F4.wireOp",EDGE,"E71.4")])]})]});
            var Q20;
            Q20=makeQuery(id+"F5.boolean.opBoolean","INTERSECT",EDGE,{"derivedFrom":[makeQuery(id+"F1.opExtrude","CAP_FACE",FACE,{"disambiguationData":[OSD([sQuery(id+"F0.wireOp",EDGE,"E45")])],"isStart":true}),makeQuery(id+"F5.opExtrude","SWEPT_FACE",FACE,{"disambiguationData":[OSD([sQuery(id+"F4.wireOp",EDGE,"E71.5")])]})]});
            var Q21;
            Q21=makeQuery(id+"F5.boolean.opBoolean","INTERSECT",EDGE,{"derivedFrom":[makeQuery(id+"F1.opExtrude","CAP_FACE",FACE,{"disambiguationData":[OSD([sQuery(id+"F0.wireOp",EDGE,"E45")])],"isStart":true}),makeQuery(id+"F5.opExtrude","SWEPT_FACE",FACE,{"disambiguationData":[OSD([sQuery(id+"F4.wireOp",EDGE,"E71.0")])]})]});
            var Q22;
            Q22=makeQuery(id+"F5.boolean.opBoolean","INTERSECT",EDGE,{"derivedFrom":[makeQuery(id+"F1.opExtrude","CAP_FACE",FACE,{"disambiguationData":[OSD([sQuery(id+"F0.wireOp",EDGE,"E45")])],"isStart":true}),makeQuery(id+"F5.opExtrude","SWEPT_FACE",FACE,{"disambiguationData":[OSD([sQuery(id+"F4.wireOp",EDGE,"E71.1")])]})]});
            var Q23;
            Q23=makeQuery(id+"F5.boolean.opBoolean","INTERSECT",EDGE,{"derivedFrom":[makeQuery(id+"F1.opExtrude","CAP_FACE",FACE,{"disambiguationData":[OSD([sQuery(id+"F0.wireOp",EDGE,"E44")])],"isStart":true}),makeQuery(id+"F5.opExtrude","SWEPT_FACE",FACE,{"disambiguationData":[OSD([sQuery(id+"F4.wireOp",EDGE,"E70.4")])]})]});
            var Q24;
            Q24=makeQuery(id+"F5.boolean.opBoolean","INTERSECT",EDGE,{"derivedFrom":[makeQuery(id+"F1.opExtrude","CAP_FACE",FACE,{"disambiguationData":[OSD([sQuery(id+"F0.wireOp",EDGE,"E44")])],"isStart":true}),makeQuery(id+"F5.opExtrude","SWEPT_FACE",FACE,{"disambiguationData":[OSD([sQuery(id+"F4.wireOp",EDGE,"E70.3")])]})]});
            var Q25;
            Q25=makeQuery(id+"F5.boolean.opBoolean","INTERSECT",EDGE,{"derivedFrom":[makeQuery(id+"F1.opExtrude","CAP_FACE",FACE,{"disambiguationData":[OSD([sQuery(id+"F0.wireOp",EDGE,"E44")])],"isStart":true}),makeQuery(id+"F5.opExtrude","SWEPT_FACE",FACE,{"disambiguationData":[OSD([sQuery(id+"F4.wireOp",EDGE,"E70.5")])]})]});
            var Q26;
            Q26=makeQuery(id+"F5.boolean.opBoolean","INTERSECT",EDGE,{"derivedFrom":[makeQuery(id+"F1.opExtrude","CAP_FACE",FACE,{"disambiguationData":[OSD([sQuery(id+"F0.wireOp",EDGE,"E44")])],"isStart":true}),makeQuery(id+"F5.opExtrude","SWEPT_FACE",FACE,{"disambiguationData":[OSD([sQuery(id+"F4.wireOp",EDGE,"E70.0")])]})]});
            var Q27;
            Q27=makeQuery(id+"F5.boolean.opBoolean","INTERSECT",EDGE,{"derivedFrom":[makeQuery(id+"F1.opExtrude","CAP_FACE",FACE,{"disambiguationData":[OSD([sQuery(id+"F0.wireOp",EDGE,"E44")])],"isStart":true}),makeQuery(id+"F5.opExtrude","SWEPT_FACE",FACE,{"disambiguationData":[OSD([sQuery(id+"F4.wireOp",EDGE,"E70.1")])]})]});
            var Q28;
            Q28=makeQuery(id+"F5.boolean.opBoolean","INTERSECT",EDGE,{"derivedFrom":[makeQuery(id+"F1.opExtrude","CAP_FACE",FACE,{"disambiguationData":[OSD([sQuery(id+"F0.wireOp",EDGE,"E44")])],"isStart":true}),makeQuery(id+"F5.opExtrude","SWEPT_FACE",FACE,{"disambiguationData":[OSD([sQuery(id+"F4.wireOp",EDGE,"E70.2")])]})]});
            var Q29;
            Q29=makeQuery(id+"F5.boolean.opBoolean","INTERSECT",EDGE,{"derivedFrom":[makeQuery(id+"F2.opExtrude","CAP_FACE",FACE,{"disambiguationData":[OSD([sQuery(id+"F0.wireOp",EDGE,"E41"),sQuery(id+"F0.wireOp",EDGE,"E42"),sQuery(id+"F0.wireOp",EDGE,"E43"),sQuery(id+"F0.wireOp",EDGE,"E44"),sQuery(id+"F0.wireOp",EDGE,"E45"),sQuery(id+"F0.wireOp",EDGE,"E54"),sQuery(id+"F0.wireOp",EDGE,"E55"),sQuery(id+"F0.wireOp",EDGE,"E56"),sQuery(id+"F0.wireOp",EDGE,"E57"),sQuery(id+"F0.wireOp",EDGE,"E58"),sQuery(id+"F0.wireOp",EDGE,"E59")])],"isStart":true}),makeQuery(id+"F5.opExtrude","SWEPT_FACE",FACE,{"disambiguationData":[OSD([sQuery(id+"F4.wireOp",EDGE,"E83")])]})]});
            var Q30;
            Q30=makeQuery(id+"F5.boolean.opBoolean","INTERSECT",EDGE,{"derivedFrom":[makeQuery(id+"F2.opExtrude","CAP_FACE",FACE,{"disambiguationData":[OSD([sQuery(id+"F0.wireOp",EDGE,"E41"),sQuery(id+"F0.wireOp",EDGE,"E42"),sQuery(id+"F0.wireOp",EDGE,"E43"),sQuery(id+"F0.wireOp",EDGE,"E44"),sQuery(id+"F0.wireOp",EDGE,"E45"),sQuery(id+"F0.wireOp",EDGE,"E54"),sQuery(id+"F0.wireOp",EDGE,"E55"),sQuery(id+"F0.wireOp",EDGE,"E56"),sQuery(id+"F0.wireOp",EDGE,"E57"),sQuery(id+"F0.wireOp",EDGE,"E58"),sQuery(id+"F0.wireOp",EDGE,"E59")])],"isStart":true}),makeQuery(id+"F5.opExtrude","SWEPT_FACE",FACE,{"disambiguationData":[OSD([sQuery(id+"F4.wireOp",EDGE,"E85")])]})]});
            var Q31;
            Q31=makeQuery(id+"F5.boolean.opBoolean","INTERSECT",EDGE,{"derivedFrom":[makeQuery(id+"F2.opExtrude","CAP_FACE",FACE,{"disambiguationData":[OSD([sQuery(id+"F0.wireOp",EDGE,"E41"),sQuery(id+"F0.wireOp",EDGE,"E42"),sQuery(id+"F0.wireOp",EDGE,"E43"),sQuery(id+"F0.wireOp",EDGE,"E44"),sQuery(id+"F0.wireOp",EDGE,"E45"),sQuery(id+"F0.wireOp",EDGE,"E54"),sQuery(id+"F0.wireOp",EDGE,"E55"),sQuery(id+"F0.wireOp",EDGE,"E56"),sQuery(id+"F0.wireOp",EDGE,"E57"),sQuery(id+"F0.wireOp",EDGE,"E58"),sQuery(id+"F0.wireOp",EDGE,"E59")])],"isStart":true}),makeQuery(id+"F5.opExtrude","SWEPT_FACE",FACE,{"disambiguationData":[OSD([sQuery(id+"F4.wireOp",EDGE,"E87")])]})]});
            var Q32;
            Q32=makeQuery(id+"F5.boolean.opBoolean","INTERSECT",EDGE,{"derivedFrom":[makeQuery(id+"F2.opExtrude","CAP_FACE",FACE,{"disambiguationData":[OSD([sQuery(id+"F0.wireOp",EDGE,"E41"),sQuery(id+"F0.wireOp",EDGE,"E42"),sQuery(id+"F0.wireOp",EDGE,"E43"),sQuery(id+"F0.wireOp",EDGE,"E44"),sQuery(id+"F0.wireOp",EDGE,"E45"),sQuery(id+"F0.wireOp",EDGE,"E54"),sQuery(id+"F0.wireOp",EDGE,"E55"),sQuery(id+"F0.wireOp",EDGE,"E56"),sQuery(id+"F0.wireOp",EDGE,"E57"),sQuery(id+"F0.wireOp",EDGE,"E58"),sQuery(id+"F0.wireOp",EDGE,"E59")])],"isStart":true}),makeQuery(id+"F5.opExtrude","SWEPT_FACE",FACE,{"disambiguationData":[OSD([sQuery(id+"F4.wireOp",EDGE,"E89")])]})]});
            var Q33;
            Q33=makeQuery(id+"F5.boolean.opBoolean","INTERSECT",EDGE,{"derivedFrom":[makeQuery(id+"F2.opExtrude","CAP_FACE",FACE,{"disambiguationData":[OSD([sQuery(id+"F0.wireOp",EDGE,"E41"),sQuery(id+"F0.wireOp",EDGE,"E42"),sQuery(id+"F0.wireOp",EDGE,"E43"),sQuery(id+"F0.wireOp",EDGE,"E44"),sQuery(id+"F0.wireOp",EDGE,"E45"),sQuery(id+"F0.wireOp",EDGE,"E54"),sQuery(id+"F0.wireOp",EDGE,"E55"),sQuery(id+"F0.wireOp",EDGE,"E56"),sQuery(id+"F0.wireOp",EDGE,"E57"),sQuery(id+"F0.wireOp",EDGE,"E58"),sQuery(id+"F0.wireOp",EDGE,"E59")])],"isStart":true}),makeQuery(id+"F5.opExtrude","SWEPT_FACE",FACE,{"disambiguationData":[OSD([sQuery(id+"F4.wireOp",EDGE,"E91")])]})]});
            var Q34;
            Q34=makeQuery(id+"F5.boolean.opBoolean","INTERSECT",EDGE,{"derivedFrom":[makeQuery(id+"F1.opExtrude","CAP_FACE",FACE,{"disambiguationData":[OSD([sQuery(id+"F0.wireOp",EDGE,"E54")])],"isStart":true}),makeQuery(id+"F5.opExtrude","SWEPT_FACE",FACE,{"disambiguationData":[OSD([sQuery(id+"F4.wireOp",EDGE,"E67")])]})]});
            chamfer(context, id + "F10", {"entities" : qUnion([Q0, Q1, Q2, Q3, Q4, Q5, Q6, Q7, Q8, Q9, Q10, Q11, Q12, Q13, Q14, Q15, Q16, Q17, Q18, Q19, Q20, Q21, Q22, Q23, Q24, Q25, Q26, Q27, Q28, Q29, Q30, Q31, Q32, Q33, Q34]), "width" : 1 * mm, "tangentPropagation" : true});
        }
    });
